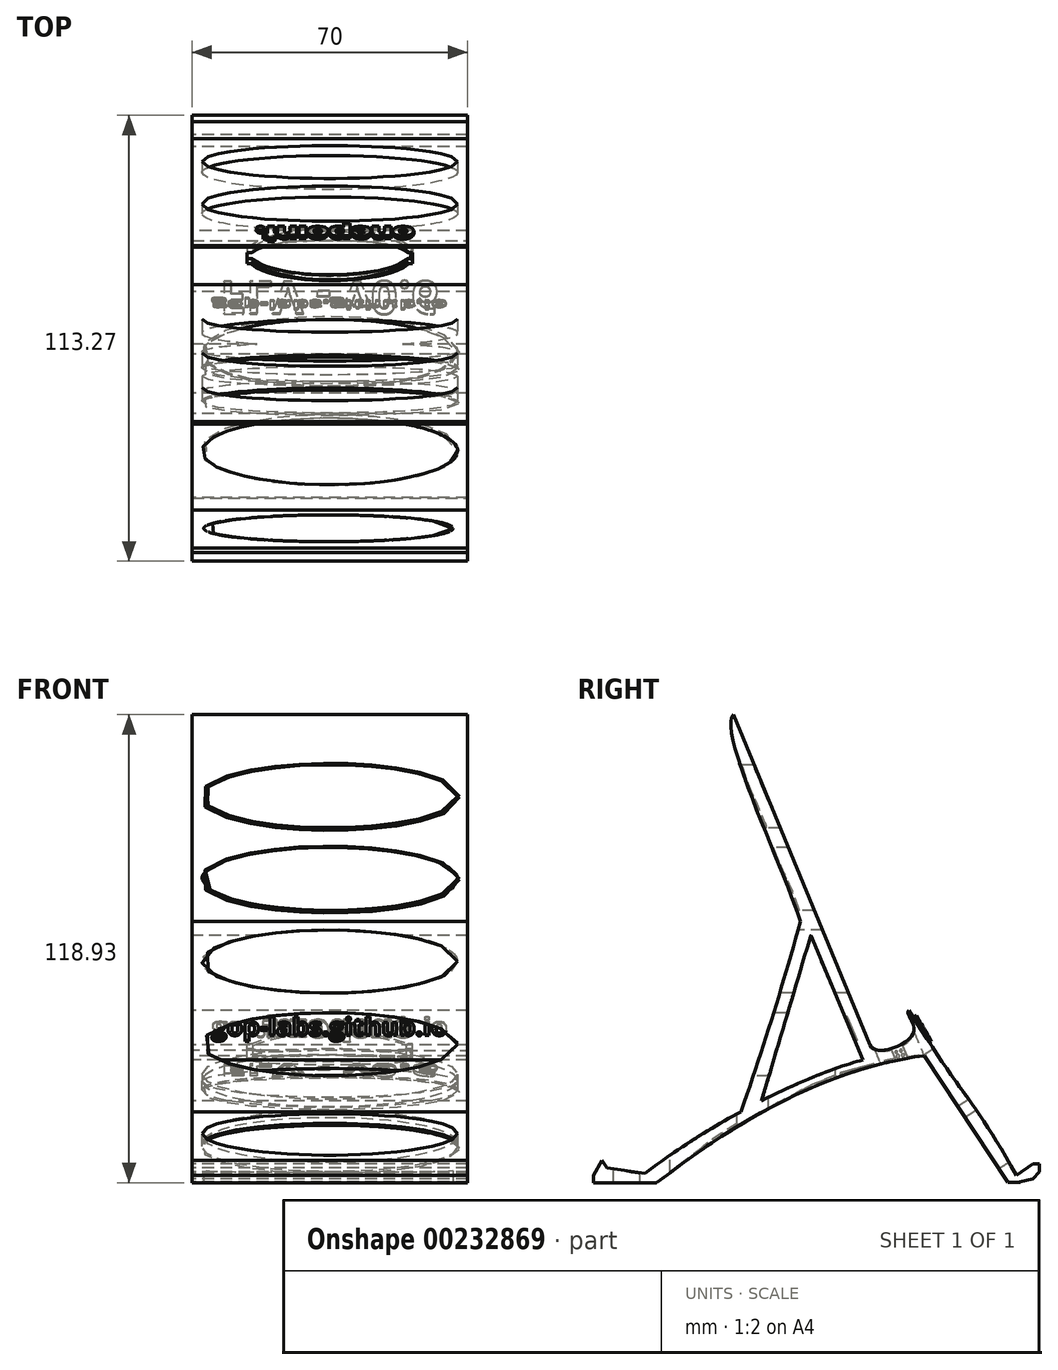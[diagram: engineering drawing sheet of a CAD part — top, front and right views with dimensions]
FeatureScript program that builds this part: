
annotation { "Feature Type Name" : "Feature", "Feature Type Description" : "" }
export const myFeature = defineFeature(function(context is Context, id is Id, definition is map)
    precondition{}
    {
        {
            var Q0;
            Q0=qCreatedBy(makeId("Right.planeOp"),FACE);
            var sketch = newSketch(context, id + "F0", { "sketchPlane" : qUnion([Q0])});
            skFitSpline(sketch, "E0", {"points": [v(42.97, 20.37) * mm, v(14.77, 64.07) * mm], "startDerivative": vector(-33.57, 62.35) * mm, "endDerivative": vector(-38.78, 64) * mm});
            skLineSegment(sketch, "E1", {"start": v(-29.92, 139.27) * mm, "end": v(4.83, 55.39) * mm});
            skFitSpline(sketch, "E2", {"points": [v(4.83, 55.39) * mm, v(15.94, 58.63) * mm, v(14.77, 64.07) * mm], "startDerivative": vector(5.7, -17.02) * mm, "endDerivative": vector(10.42, 3.26) * mm});
            skLineSegment(sketch, "E3", {"start": v(18.6, 52.58) * mm, "end": v(39.9, 20.37) * mm});
            skLineSegment(sketch, "E4", {"start": v(-10.23, 83.1) * mm, "end": v(3.1, 51.52) * mm});
            skFitSpline(sketch, "E5", {"points": [v(-29.92, 139.27) * mm, v(-12.82, 86.66) * mm], "startDerivative": vector(-12.17, -12.55) * mm, "endDerivative": vector(13.11, -40.92) * mm});
            skFitSpline(sketch, "E6", {"points": [v(3.1, 51.52) * mm, v(-55.3, 20.37) * mm], "startDerivative": vector(-34.97, -8.7) * mm, "endDerivative": vector(-63.71, -51.04) * mm});
            skFitSpline(sketch, "E7", {"points": [v(18.6, 52.58) * mm, v(-49.24, 20.37) * mm], "startDerivative": vector(-55.78, -6.95) * mm, "endDerivative": vector(-79.56, -62.3) * mm});
            skLineSegment(sketch, "E8", {"start": v(-49.24, 20.37) * mm, "end": v(-55.3, 20.37) * mm});
            skLineSegment(sketch, "E9", {"start": v(42.97, 20.37) * mm, "end": v(39.9, 20.37) * mm});
            skLineSegment(sketch, "E10", {"start": v(39.9, 20.37) * mm, "end": v(-49.24, 20.37) * mm});
            skFitSpline(sketch, "E11", {"points": [v(-10.23, 83.1) * mm, v(-22.72, 41.14) * mm], "startDerivative": vector(-11.4, -38.7) * mm, "endDerivative": vector(-11.4, -38.7) * mm});
            skFitSpline(sketch, "E12", {"points": [v(-12.82, 86.66) * mm, v(-27.98, 38.37) * mm], "startDerivative": vector(-14.28, -50.37) * mm, "endDerivative": vector(-17.92, -50.53) * mm});
            skSolve(sketch);
        }
        {
            var Q0;
            Q0=makeQuery(id+"F0.imprint","IMPRINT",FACE,{"disambiguationData":[TD([[makeQuery(id+"F0.imprint","IMPRINT",EDGE,{"derivedFrom":sQuery(id+"F0.wireOp",EDGE,"e2dd9e04-bce8-43ee-a2f2-a46b7d135692")}),-1.0]])]});
            var Q1;
            Q1=makeQuery(id+"F0.imprint","IMPRINT",FACE,{"disambiguationData":[TD([[makeQuery(id+"F0.imprint","IMPRINT",EDGE,{"derivedFrom":sQuery(id+"F0.wireOp",EDGE,"dd02e322-1caa-4adf-9807-8f987be65d11")}),1.0]])]});
            var Q2;
            Q2=makeQuery(id+"F0.imprint","IMPRINT",FACE,{"disambiguationData":[TD([[makeQuery(id+"F0.imprint","IMPRINT",EDGE,{"derivedFrom":sQuery(id+"F0.wireOp",EDGE,"E0")}),1.0]])]});
            var Q3;
            {var subQ0=sQuery(id+"F0.wireOp",EDGE,"E6");Q3=makeQuery(id+"F0.imprint","IMPRINT",FACE,{"disambiguationData":[TD([[makeQuery(id+"F0.imprint","IMPRINT",EDGE,{"derivedFrom":subQ0}),1.0]])]});}
            extrude(context, id + "F1", {"entities" : qUnion([Q0, Q1, Q2, Q3]), "depth" : 70 * mm});
        }
        {
            var Q0;
            Q0=makeQuery(id+"F1.opExtrude","SWEPT_FACE",FACE,{"disambiguationData":[OSD([sQuery(id+"F0.wireOp",EDGE,"E3")])]});
            var sketch = newSketch(context, id + "F2", { "sketchPlane" : qUnion([Q0])});
            skEllipse(sketch, "E13", {"center": v(35, 25.97) * mm, "majorRadius": 32.5 * mm, "minorRadius": 7.82 * mm, "majorAxis": v(1, 0)});
            skEllipse(sketch, "E14.0.1.0", {"center": v(35, 6.97) * mm, "majorRadius": 32.5 * mm, "minorRadius": 7.82 * mm, "majorAxis": v(1, 0)});
            skLineSegment(sketch, "E14.direction1", {"start": v(35, 25.97) * mm, "end": v(57.03, 25.97) * mm, "construction": true});
            skLineSegment(sketch, "E14.direction2", {"start": v(35, 25.97) * mm, "end": v(35, 6.97) * mm, "construction": true});
            skSolve(sketch);
        }
        {
            var Q0;
            Q0=qSketchRegion(id+"F2",true);
            var Q1;
            Q1=makeQuery(id+"F1.opExtrude","SWEPT_FACE",FACE,{"disambiguationData":[OSD([sQuery(id+"F0.wireOp",EDGE,"E0")])]});
            extrude(context, id + "F3", {"entities" : qUnion([Q0]), "operationType" : NewBodyOperationType.REMOVE, "endBound" : BoundingType.UP_TO_SURFACE, "oppositeDirection" : true, "endBoundEntityFace" : qUnion([Q1]), "depth" : 25 * mm});
        }
        {
            var Q0;
            Q0=qCreatedBy(makeId("Top.planeOp"),FACE);
            var sketch = newSketch(context, id + "F4", { "sketchPlane" : qUnion([Q0])});
            skEllipse(sketch, "E15", {"center": v(35, -37.48) * mm, "majorRadius": 32.5 * mm, "minorRadius": 8.5 * mm, "majorAxis": v(1, 0)});
            skEllipse(sketch, "E16.0.1.0", {"center": v(35, -12.48) * mm, "majorRadius": 32.5 * mm, "minorRadius": 8.5 * mm, "majorAxis": v(1, 0)});
            skLineSegment(sketch, "E16.direction1", {"start": v(35, -37.48) * mm, "end": v(60, -37.48) * mm, "construction": true});
            skLineSegment(sketch, "E16.direction2", {"start": v(35, -37.48) * mm, "end": v(35, -12.48) * mm, "construction": true});
            skSolve(sketch);
        }
        {
            var Q0;
            Q0=makeQuery(id+"F4.imprint","IMPRINT",FACE,{"disambiguationData":[TD([[makeQuery(id+"F4.imprint","IMPRINT",EDGE,{"derivedFrom":sQuery(id+"F4.wireOp",EDGE,"E16.0.1.0")}),1.0]])]});
            var Q1;
            Q1=makeQuery(id+"F4.imprint","IMPRINT",FACE,{"disambiguationData":[TD([[makeQuery(id+"F4.imprint","IMPRINT",EDGE,{"derivedFrom":sQuery(id+"F4.wireOp",EDGE,"E16.0.2.0")}),1.0]])]});
            var Q2;
            Q2=makeQuery(id+"F1.opExtrude","SWEPT_FACE",FACE,{"disambiguationData":[OSD([sQuery(id+"F0.wireOp",EDGE,"E6")])]});
            extrude(context, id + "F5", {"entities" : qUnion([Q0, Q1]), "operationType" : NewBodyOperationType.REMOVE, "endBound" : BoundingType.UP_TO_SURFACE, "endBoundEntityFace" : qUnion([Q2]), "depth" : 25 * mm});
        }
        {
            var Q0;
            Q0=qCreatedBy(makeId("Front.planeOp"),FACE);
            cPlane(context, id + "F6", {"entities" : qUnion([Q0]), "cplaneType" : CPlaneType.OFFSET, "offset" : 70 * mm, "width" : 150 * mm, "height" : 150 * mm});
        }
        {
            var Q0;
            Q0=qCreatedBy(id+"F6.planeOp",FACE);
            var sketch = newSketch(context, id + "F7", { "sketchPlane" : qUnion([Q0])});
            skEllipse(sketch, "E17", {"center": v(35, 118.52) * mm, "majorRadius": 32.5 * mm, "minorRadius": 8 * mm, "majorAxis": v(1, 0)});
            skEllipse(sketch, "E18.0.1.0", {"center": v(35, 97.52) * mm, "majorRadius": 32.5 * mm, "minorRadius": 8 * mm, "majorAxis": v(1, 0)});
            skEllipse(sketch, "E18.0.2.0", {"center": v(35, 76.52) * mm, "majorRadius": 32.5 * mm, "minorRadius": 8 * mm, "majorAxis": v(1, 0)});
            skEllipse(sketch, "E18.0.3.0", {"center": v(35, 55.52) * mm, "majorRadius": 32.5 * mm, "minorRadius": 8 * mm, "majorAxis": v(1, 0)});
            skEllipse(sketch, "E18.0.4.0", {"center": v(35, 34.52) * mm, "majorRadius": 32.5 * mm, "minorRadius": 8 * mm, "majorAxis": v(1, 0)});
            skEllipse(sketch, "E18.0.5.0", {"center": v(35, 13.52) * mm, "majorRadius": 32.5 * mm, "minorRadius": 8 * mm, "majorAxis": v(1, 0)});
            skLineSegment(sketch, "E18.direction1", {"start": v(35, 118.52) * mm, "end": v(60, 118.52) * mm, "construction": true});
            skLineSegment(sketch, "E18.direction2", {"start": v(35, 118.52) * mm, "end": v(35, 97.52) * mm, "construction": true});
            skSolve(sketch);
        }
        {
            var Q0;
            Q0=makeQuery(id+"F7.imprint","IMPRINT",FACE,{"disambiguationData":[TD([[makeQuery(id+"F7.imprint","IMPRINT",EDGE,{"derivedFrom":sQuery(id+"F7.wireOp",EDGE,"E18.0.3.0")}),1.0]])]});
            var Q1;
            Q1=makeQuery(id+"F1.opExtrude","SWEPT_FACE",FACE,{"disambiguationData":[OSD([sQuery(id+"F0.wireOp",EDGE,"E11")])]});
            extrude(context, id + "F8", {"entities" : qUnion([Q0]), "operationType" : NewBodyOperationType.REMOVE, "endBound" : BoundingType.UP_TO_SURFACE, "oppositeDirection" : true, "endBoundEntityFace" : qUnion([Q1]), "depth" : 25 * mm});
        }
        {
            var Q0;
            Q0=makeQuery(id+"F7.imprint","IMPRINT",FACE,{"disambiguationData":[TD([[makeQuery(id+"F7.imprint","IMPRINT",EDGE,{"derivedFrom":sQuery(id+"F7.wireOp",EDGE,"E17")}),1.0]])]});
            var Q1;
            Q1=makeQuery(id+"F7.imprint","IMPRINT",FACE,{"disambiguationData":[TD([[makeQuery(id+"F7.imprint","IMPRINT",EDGE,{"derivedFrom":sQuery(id+"F7.wireOp",EDGE,"E18.0.1.0")}),1.0]])]});
            var Q2;
            Q2=makeQuery(id+"F7.imprint","IMPRINT",FACE,{"disambiguationData":[TD([[makeQuery(id+"F7.imprint","IMPRINT",EDGE,{"derivedFrom":sQuery(id+"F7.wireOp",EDGE,"E18.0.2.0")}),1.0]])]});
            var Q3;
            Q3=makeQuery(id+"F1.opExtrude","SWEPT_FACE",FACE,{"disambiguationData":[OSD([sQuery(id+"F0.wireOp",EDGE,"E1")])]});
            extrude(context, id + "F9", {"entities" : qUnion([Q0, Q1, Q2]), "operationType" : NewBodyOperationType.REMOVE, "endBound" : BoundingType.UP_TO_SURFACE, "oppositeDirection" : true, "endBoundEntityFace" : qUnion([Q3]), "depth" : 25 * mm});
        }
        {
            var Q0;
            Q0=makeQuery(id+"F1.opExtrude","SWEPT_FACE",FACE,{"disambiguationData":[OSD([sQuery(id+"F0.wireOp",EDGE,"E1")])]});
            var Q1;
            Q1=makeQuery(id+"F1.opExtrude","SWEPT_EDGE",EDGE,{"disambiguationData":[OSD([sQuery(id+"F0.wireOp",EDGE,"E1"),sQuery(id+"F0.wireOp",EDGE,"E5")])]});
            cPlane(context, id + "F10", {"entities" : qUnion([Q0, Q1]), "cplaneType" : CPlaneType.LINE_ANGLE, "offset" : 25 * mm, "angle" : 90 * degree, "width" : 150 * mm, "height" : 150 * mm});
        }
        {
            var Q0;
            Q0=qCreatedBy(id+"F10.planeOp",FACE);
            var sketch = newSketch(context, id + "F11", { "sketchPlane" : qUnion([Q0])});
            skEllipse(sketch, "E19", {"center": v(35, 31.76) * mm, "majorRadius": 20.25 * mm, "minorRadius": 5.5 * mm, "majorAxis": v(-1, 0)});
            skLineSegment(sketch, "E20.bottom", {"start": v(14, 30.26) * mm, "end": v(56, 30.26) * mm});
            skLineSegment(sketch, "E20.top", {"start": v(14, 33.26) * mm, "end": v(56, 33.26) * mm});
            skLineSegment(sketch, "E20.left", {"start": v(14, 30.26) * mm, "end": v(14, 33.26) * mm});
            skLineSegment(sketch, "E20.right", {"start": v(56, 30.26) * mm, "end": v(56, 33.26) * mm});
            skSolve(sketch);
        }
        {
            var Q0;
            Q0=qSketchRegion(id+"F11",true);
            var Q1;
            Q1=makeQuery(id+"F1.opExtrude","SWEPT_FACE",FACE,{"disambiguationData":[OSD([sQuery(id+"F0.wireOp",EDGE,"E7")])]});
            extrude(context, id + "F12", {"entities" : qUnion([Q0]), "operationType" : NewBodyOperationType.REMOVE, "endBound" : BoundingType.THROUGH_ALL, "oppositeDirection" : true, "endBoundEntityFace" : qUnion([Q1]), "depth" : 25 * mm});
        }
        {
            var Q0;
            Q0=makeQuery(id+"F3.boolean.opBoolean","COPY",EDGE,{"derivedFrom":makeQuery(id+"F3.opExtrude","TWEAK_EDGE",EDGE,{"derivedFrom":[makeQuery(id+"F1.opExtrude","SWEPT_FACE",FACE,{"disambiguationData":[OSD([sQuery(id+"F0.wireOp",EDGE,"E0")])]}),makeQuery(id+"F2.imprint","IMPRINT",EDGE,{"derivedFrom":sQuery(id+"F2.wireOp",EDGE,"E13")})]})});
            var Q1;
            Q1=makeQuery(id+"F3.boolean.opBoolean","COPY",EDGE,{"derivedFrom":makeQuery(id+"F3.opExtrude","TWEAK_EDGE",EDGE,{"derivedFrom":[makeQuery(id+"F1.opExtrude","SWEPT_FACE",FACE,{"disambiguationData":[OSD([sQuery(id+"F0.wireOp",EDGE,"E0")])]}),makeQuery(id+"F2.imprint","IMPRINT",EDGE,{"derivedFrom":sQuery(id+"F2.wireOp",EDGE,"E14.0.1.0")})]})});
            var Q2;
            Q2=makeQuery(id+"F3.boolean.opBoolean","COPY",EDGE,{"derivedFrom":makeQuery(id+"F3.opExtrude","TWEAK_EDGE",EDGE,{"derivedFrom":[makeQuery(id+"F1.opExtrude","SWEPT_FACE",FACE,{"disambiguationData":[OSD([sQuery(id+"F0.wireOp",EDGE,"E0")])]}),makeQuery(id+"F2.imprint","IMPRINT",EDGE,{"derivedFrom":sQuery(id+"F2.wireOp",EDGE,"E14.0.2.0")})]})});
            var Q3;
            Q3=makeQuery(id+"F3.boolean.opBoolean","COPY",EDGE,{"derivedFrom":makeQuery(id+"F3.opExtrude","CAP_EDGE",EDGE,{"disambiguationData":[OSD([sQuery(id+"F2.wireOp",EDGE,"E13")])],"isStart":true})});
            var Q4;
            Q4=makeQuery(id+"F3.boolean.opBoolean","COPY",EDGE,{"derivedFrom":makeQuery(id+"F3.opExtrude","CAP_EDGE",EDGE,{"disambiguationData":[OSD([sQuery(id+"F2.wireOp",EDGE,"E14.0.1.0")])],"isStart":true})});
            var Q5;
            Q5=makeQuery(id+"F3.boolean.opBoolean","COPY",EDGE,{"derivedFrom":makeQuery(id+"F3.opExtrude","CAP_EDGE",EDGE,{"disambiguationData":[OSD([sQuery(id+"F2.wireOp",EDGE,"E14.0.2.0")])],"isStart":true})});
            var Q6;
            Q6=makeQuery(id+"F8.boolean.opBoolean","INTERSECT",EDGE,{"derivedFrom":[makeQuery(id+"F1.opExtrude","SWEPT_FACE",FACE,{"disambiguationData":[OSD([sQuery(id+"F0.wireOp",EDGE,"61fd75d5-24df-4c68-a095-90f6d82b9ead")])]}),makeQuery(id+"F8.opExtrude","SWEPT_FACE",FACE,{"disambiguationData":[OSD([sQuery(id+"F7.wireOp",EDGE,"E18.0.3.0")])]})]});
            var Q7;
            Q7=makeQuery(id+"F8.boolean.opBoolean","COPY",EDGE,{"derivedFrom":makeQuery(id+"F8.opExtrude","CAP_EDGE",EDGE,{"disambiguationData":[OSD([sQuery(id+"F7.wireOp",EDGE,"E18.0.3.0")])],"isStart":false})});
            var Q8;
            Q8=makeQuery(id+"F8.boolean.opBoolean","INTERSECT",EDGE,{"derivedFrom":[makeQuery(id+"F1.opExtrude","SWEPT_FACE",FACE,{"disambiguationData":[OSD([sQuery(id+"F0.wireOp",EDGE,"61fd75d5-24df-4c68-a095-90f6d82b9ead")])]}),makeQuery(id+"F8.opExtrude","SWEPT_FACE",FACE,{"disambiguationData":[OSD([sQuery(id+"F7.wireOp",EDGE,"E18.0.4.0")])]})]});
            var Q9;
            {var subQ0=sQuery(id+"F0.wireOp",EDGE,"5998eb2a-c125-4484-9ba4-89ed062cae3a");var subQ1=sQuery(id+"F0.wireOp",EDGE,"E7");var subQ2=sQuery(id+"F7.wireOp",EDGE,"E18.0.4.0");Q9=makeQuery(id+"F8.boolean.opBoolean","COPY",EDGE,{"disambiguationData":[TD([makeQuery(id+"F1.opExtrude","SWEPT_FACE",FACE,{"disambiguationData":[OSD([subQ0]),TDD([makeQuery(id+"F0.imprint","IMPRINT",EDGE,{"disambiguationData":[TD([[makeQuery(id+"F0.imprint","INTERSECT",VERTEX,{"derivedFrom":[subQ0,sQuery(id+"F0.wireOp",EDGE,"umK4nLRB-749r-FOEl-6r3i-m92kNIwFStfI")]}),-1.0]])],"derivedFrom":subQ0})])]}),makeQuery(id+"F1.opExtrude","SWEPT_FACE",FACE,{"disambiguationData":[OSD([subQ1])]}),makeQuery(id+"F8.opExtrude","SWEPT_FACE",FACE,{"disambiguationData":[OSD([subQ2])]}),makeQuery(id+"F8.opExtrude","CAP_FACE",FACE,{"disambiguationData":[OSD([subQ2])],"isStart":false})])],"derivedFrom":makeQuery(id+"F8.opExtrude","CAP_EDGE",EDGE,{"disambiguationData":[OSD([subQ2])],"isStart":false})});}
            var Q10;
            Q10=makeQuery(id+"F8.boolean.opBoolean","INTERSECT",EDGE,{"derivedFrom":[makeQuery(id+"F1.opExtrude","SWEPT_FACE",FACE,{"disambiguationData":[OSD([sQuery(id+"F0.wireOp",EDGE,"61fd75d5-24df-4c68-a095-90f6d82b9ead")])]}),makeQuery(id+"F8.opExtrude","SWEPT_FACE",FACE,{"disambiguationData":[OSD([sQuery(id+"F7.wireOp",EDGE,"E18.0.5.0")])]})]});
            var Q11;
            Q11=makeQuery(id+"F8.boolean.opBoolean","COPY",EDGE,{"derivedFrom":makeQuery(id+"F8.opExtrude","CAP_EDGE",EDGE,{"disambiguationData":[OSD([sQuery(id+"F7.wireOp",EDGE,"E18.0.5.0")])],"isStart":false})});
            var Q12;
            {var subQ0=sQuery(id+"F0.wireOp",EDGE,"5998eb2a-c125-4484-9ba4-89ed062cae3a");Q12=makeQuery(id+"F9.boolean.opBoolean","INTERSECT",EDGE,{"derivedFrom":[makeQuery(id+"F1.opExtrude","SWEPT_FACE",FACE,{"disambiguationData":[OSD([subQ0]),TDD([makeQuery(id+"F0.imprint","IMPRINT",EDGE,{"disambiguationData":[TD([[makeQuery(id+"F0.imprint","INTERSECT",VERTEX,{"derivedFrom":[subQ0,sQuery(id+"F0.wireOp",EDGE,"E4")]}),1.0]])],"derivedFrom":subQ0})])]}),makeQuery(id+"F9.opExtrude","SWEPT_FACE",FACE,{"disambiguationData":[OSD([sQuery(id+"F7.wireOp",EDGE,"E18.0.2.0")])]})]});}
            var Q13;
            Q13=makeQuery(id+"F9.boolean.opBoolean","INTERSECT",EDGE,{"derivedFrom":[makeQuery(id+"F1.opExtrude","SWEPT_FACE",FACE,{"disambiguationData":[OSD([sQuery(id+"F0.wireOp",EDGE,"61fd75d5-24df-4c68-a095-90f6d82b9ead")])]}),makeQuery(id+"F9.opExtrude","SWEPT_FACE",FACE,{"disambiguationData":[OSD([sQuery(id+"F7.wireOp",EDGE,"E18.0.2.0")])]})]});
            var Q14;
            Q14=makeQuery(id+"F5.boolean.opBoolean","COPY",EDGE,{"derivedFrom":makeQuery(id+"F5.opExtrude","TWEAK_EDGE",EDGE,{"derivedFrom":[makeQuery(id+"F1.opExtrude","SWEPT_FACE",FACE,{"disambiguationData":[OSD([sQuery(id+"F0.wireOp",EDGE,"E6")])]}),makeQuery(id+"F4.imprint","IMPRINT",EDGE,{"derivedFrom":sQuery(id+"F4.wireOp",EDGE,"E16.0.1.0")})]})});
            var Q15;
            Q15=makeQuery(id+"F5.boolean.opBoolean","INTERSECT",EDGE,{"derivedFrom":[makeQuery(id+"F1.opExtrude","SWEPT_FACE",FACE,{"disambiguationData":[OSD([sQuery(id+"F0.wireOp",EDGE,"E7")])]}),makeQuery(id+"F5.opExtrude","SWEPT_FACE",FACE,{"disambiguationData":[OSD([sQuery(id+"F4.wireOp",EDGE,"E16.0.1.0")])]})]});
            var Q16;
            Q16=makeQuery(id+"F5.boolean.opBoolean","INTERSECT",EDGE,{"derivedFrom":[makeQuery(id+"F1.opExtrude","SWEPT_FACE",FACE,{"disambiguationData":[OSD([sQuery(id+"F0.wireOp",EDGE,"E7")])]}),makeQuery(id+"F5.opExtrude","SWEPT_FACE",FACE,{"disambiguationData":[OSD([sQuery(id+"F4.wireOp",EDGE,"E15")])]})]});
            var Q17;
            Q17=makeQuery(id+"F5.boolean.opBoolean","COPY",EDGE,{"derivedFrom":makeQuery(id+"F5.opExtrude","TWEAK_EDGE",EDGE,{"derivedFrom":[makeQuery(id+"F1.opExtrude","SWEPT_FACE",FACE,{"disambiguationData":[OSD([sQuery(id+"F0.wireOp",EDGE,"E6")])]}),makeQuery(id+"F4.imprint","IMPRINT",EDGE,{"derivedFrom":sQuery(id+"F4.wireOp",EDGE,"E15")})]})});
            var Q18;
            Q18=makeQuery(id+"F9.boolean.opBoolean","COPY",EDGE,{"derivedFrom":makeQuery(id+"F9.opExtrude","TWEAK_EDGE",EDGE,{"derivedFrom":[makeQuery(id+"F1.opExtrude","SWEPT_FACE",FACE,{"disambiguationData":[OSD([sQuery(id+"F0.wireOp",EDGE,"E1")])]}),makeQuery(id+"F7.imprint","IMPRINT",EDGE,{"derivedFrom":sQuery(id+"F7.wireOp",EDGE,"E18.0.2.0")})]})});
            var Q19;
            Q19=makeQuery(id+"F9.boolean.opBoolean","COPY",EDGE,{"derivedFrom":makeQuery(id+"F9.opExtrude","TWEAK_EDGE",EDGE,{"derivedFrom":[makeQuery(id+"F1.opExtrude","SWEPT_FACE",FACE,{"disambiguationData":[OSD([sQuery(id+"F0.wireOp",EDGE,"E1")])]}),makeQuery(id+"F7.imprint","IMPRINT",EDGE,{"derivedFrom":sQuery(id+"F7.wireOp",EDGE,"E18.0.1.0")})]})});
            var Q20;
            Q20=makeQuery(id+"F9.boolean.opBoolean","INTERSECT",EDGE,{"derivedFrom":[makeQuery(id+"F1.opExtrude","SWEPT_FACE",FACE,{"disambiguationData":[OSD([sQuery(id+"F0.wireOp",EDGE,"E5")])]}),makeQuery(id+"F9.opExtrude","SWEPT_FACE",FACE,{"disambiguationData":[OSD([sQuery(id+"F7.wireOp",EDGE,"E18.0.1.0")])]})]});
            var Q21;
            Q21=makeQuery(id+"F9.boolean.opBoolean","INTERSECT",EDGE,{"derivedFrom":[makeQuery(id+"F1.opExtrude","SWEPT_FACE",FACE,{"disambiguationData":[OSD([sQuery(id+"F0.wireOp",EDGE,"E5")])]}),makeQuery(id+"F9.opExtrude","SWEPT_FACE",FACE,{"disambiguationData":[OSD([sQuery(id+"F7.wireOp",EDGE,"E17")])]})]});
            var Q22;
            Q22=makeQuery(id+"F9.boolean.opBoolean","COPY",EDGE,{"derivedFrom":makeQuery(id+"F9.opExtrude","TWEAK_EDGE",EDGE,{"derivedFrom":[makeQuery(id+"F1.opExtrude","SWEPT_FACE",FACE,{"disambiguationData":[OSD([sQuery(id+"F0.wireOp",EDGE,"E1")])]}),makeQuery(id+"F7.imprint","IMPRINT",EDGE,{"derivedFrom":sQuery(id+"F7.wireOp",EDGE,"E17")})]})});
            fillet(context, id + "F13", {"entities" : qUnion([Q0, Q1, Q2, Q3, Q4, Q5, Q6, Q7, Q8, Q9, Q10, Q11, Q12, Q13, Q14, Q15, Q16, Q17, Q18, Q19, Q20, Q21, Q22]), "radius" : 0.5 * mm, "tangentPropagation" : true, "allowEdgeOverflow" : false});
        }
        {
            var Q0;
            Q0=makeQuery(id+"F1.opExtrude","SWEPT_EDGE",EDGE,{"disambiguationData":[OSD([sQuery(id+"F0.wireOp",EDGE,"E0"),sQuery(id+"F0.wireOp",EDGE,"E2")])]});
            cPlane(context, id + "F14", {"entities" : qUnion([Q0]), "cplaneType" : CPlaneType.LINE_ANGLE, "offset" : 25 * mm, "angle" : 150 * degree, "width" : 150 * mm, "height" : 150 * mm});
        }
        {
            var Q0;
            Q0=qCreatedBy(id+"F14.planeOp",FACE);
            var sketch = newSketch(context, id + "F15", { "sketchPlane" : qUnion([Q0])});
            skLineSegment(sketch, "E21", {"start": v(-54.12, 39.93) * mm, "end": v(-54.9, 40.17) * mm});
            skLineSegment(sketch, "E22", {"start": v(-54.9, 40.17) * mm, "end": v(-55.54, 40.6) * mm});
            skLineSegment(sketch, "E23", {"start": v(-55.54, 40.6) * mm, "end": v(-56.02, 41.2) * mm});
            skLineSegment(sketch, "E24", {"start": v(-56.02, 41.2) * mm, "end": v(-56.3, 41.94) * mm});
            skLineSegment(sketch, "E25", {"start": v(-56.3, 41.94) * mm, "end": v(-56.33, 42.13) * mm});
            skLineSegment(sketch, "E26", {"start": v(-56.33, 42.13) * mm, "end": v(-56.34, 42.37) * mm});
            skLineSegment(sketch, "E27", {"start": v(-56.34, 42.62) * mm, "end": v(-56.32, 42.83) * mm});
            skLineSegment(sketch, "E28", {"start": v(-56.32, 42.83) * mm, "end": v(-56.06, 43.6) * mm});
            skLineSegment(sketch, "E29", {"start": v(-56.06, 43.6) * mm, "end": v(-55.56, 44.26) * mm});
            skLineSegment(sketch, "E30", {"start": v(-55.56, 44.26) * mm, "end": v(-55.18, 44.57) * mm});
            skLineSegment(sketch, "E31", {"start": v(-55.18, 44.57) * mm, "end": v(-54.75, 44.8) * mm});
            skLineSegment(sketch, "E32", {"start": v(-54.75, 44.8) * mm, "end": v(-54.28, 44.94) * mm});
            skLineSegment(sketch, "E33", {"start": v(-54.28, 44.94) * mm, "end": v(-53.77, 45) * mm});
            skLineSegment(sketch, "E34", {"start": v(-53.77, 45) * mm, "end": v(-53.19, 44.98) * mm});
            skLineSegment(sketch, "E35", {"start": v(-53.19, 44.98) * mm, "end": v(-52.64, 44.84) * mm});
            skLineSegment(sketch, "E36", {"start": v(-52.64, 44.84) * mm, "end": v(-52.15, 44.6) * mm});
            skLineSegment(sketch, "E37", {"start": v(-52.15, 44.6) * mm, "end": v(-51.7, 44.26) * mm});
            skLineSegment(sketch, "E38", {"start": v(-51.7, 44.26) * mm, "end": v(-51.23, 43.63) * mm});
            skLineSegment(sketch, "E39", {"start": v(-51.23, 43.63) * mm, "end": v(-50.98, 42.9) * mm});
            skLineSegment(sketch, "E40", {"start": v(-50.98, 42.9) * mm, "end": v(-50.95, 42.7) * mm});
            skLineSegment(sketch, "E41", {"start": v(-50.95, 42.7) * mm, "end": v(-50.95, 42.45) * mm});
            skLineSegment(sketch, "E42", {"start": v(-50.95, 42.45) * mm, "end": v(-50.96, 42.2) * mm});
            skLineSegment(sketch, "E43", {"start": v(-50.96, 42.2) * mm, "end": v(-50.99, 42) * mm});
            skLineSegment(sketch, "E44", {"start": v(-50.99, 42) * mm, "end": v(-51.26, 41.25) * mm});
            skLineSegment(sketch, "E45", {"start": v(-51.26, 41.25) * mm, "end": v(-51.73, 40.64) * mm});
            skLineSegment(sketch, "E46", {"start": v(-51.73, 40.64) * mm, "end": v(-52.37, 40.19) * mm});
            skLineSegment(sketch, "E47", {"start": v(-52.37, 40.19) * mm, "end": v(-53.14, 39.94) * mm});
            skLineSegment(sketch, "E48", {"start": v(-53.14, 39.94) * mm, "end": v(-53.63, 39.9) * mm});
            skLineSegment(sketch, "E49", {"start": v(-53.63, 39.9) * mm, "end": v(-54.12, 39.93) * mm});
            skLineSegment(sketch, "E50", {"start": v(-54.12, 39.93) * mm, "end": v(-54.12, 39.93) * mm});
            skLineSegment(sketch, "E51", {"start": v(-53.38, 41.4) * mm, "end": v(-53.15, 41.5) * mm});
            skLineSegment(sketch, "E52", {"start": v(-53.15, 41.5) * mm, "end": v(-52.96, 41.63) * mm});
            skLineSegment(sketch, "E53", {"start": v(-52.96, 41.63) * mm, "end": v(-52.8, 41.82) * mm});
            skLineSegment(sketch, "E54", {"start": v(-52.8, 41.82) * mm, "end": v(-52.7, 42.06) * mm});
            skLineSegment(sketch, "E55", {"start": v(-52.7, 42.06) * mm, "end": v(-52.63, 42.42) * mm});
            skLineSegment(sketch, "E56", {"start": v(-52.63, 42.42) * mm, "end": v(-52.67, 42.77) * mm});
            skLineSegment(sketch, "E57", {"start": v(-52.67, 42.77) * mm, "end": v(-52.8, 43.04) * mm});
            skLineSegment(sketch, "E58", {"start": v(-52.8, 43.04) * mm, "end": v(-52.97, 43.26) * mm});
            skLineSegment(sketch, "E59", {"start": v(-52.97, 43.26) * mm, "end": v(-53.2, 43.42) * mm});
            skLineSegment(sketch, "E60", {"start": v(-53.2, 43.42) * mm, "end": v(-53.46, 43.52) * mm});
            skLineSegment(sketch, "E61", {"start": v(-53.46, 43.52) * mm, "end": v(-53.57, 43.54) * mm});
            skLineSegment(sketch, "E62", {"start": v(-53.57, 43.54) * mm, "end": v(-53.66, 43.55) * mm});
            skLineSegment(sketch, "E63", {"start": v(-53.66, 43.55) * mm, "end": v(-53.88, 43.52) * mm});
            skLineSegment(sketch, "E64", {"start": v(-53.88, 43.52) * mm, "end": v(-54.1, 43.44) * mm});
            skLineSegment(sketch, "E65", {"start": v(-54.1, 43.44) * mm, "end": v(-54.28, 43.32) * mm});
            skLineSegment(sketch, "E66", {"start": v(-54.28, 43.32) * mm, "end": v(-54.43, 43.16) * mm});
            skLineSegment(sketch, "E67", {"start": v(-54.43, 43.16) * mm, "end": v(-54.55, 42.97) * mm});
            skLineSegment(sketch, "E68", {"start": v(-54.55, 42.97) * mm, "end": v(-54.62, 42.76) * mm});
            skLineSegment(sketch, "E69", {"start": v(-54.62, 42.76) * mm, "end": v(-54.65, 42.62) * mm});
            skLineSegment(sketch, "E70", {"start": v(-54.65, 42.62) * mm, "end": v(-54.66, 42.46) * mm});
            skLineSegment(sketch, "E71", {"start": v(-54.66, 42.46) * mm, "end": v(-54.65, 42.3) * mm});
            skLineSegment(sketch, "E72", {"start": v(-54.65, 42.3) * mm, "end": v(-54.62, 42.18) * mm});
            skLineSegment(sketch, "E73", {"start": v(-54.62, 42.18) * mm, "end": v(-54.52, 41.9) * mm});
            skLineSegment(sketch, "E74", {"start": v(-54.52, 41.9) * mm, "end": v(-54.35, 41.68) * mm});
            skLineSegment(sketch, "E75", {"start": v(-54.35, 41.68) * mm, "end": v(-54.14, 41.5) * mm});
            skLineSegment(sketch, "E76", {"start": v(-54.14, 41.5) * mm, "end": v(-53.89, 41.4) * mm});
            skLineSegment(sketch, "E77", {"start": v(-53.89, 41.4) * mm, "end": v(-53.64, 41.37) * mm});
            skLineSegment(sketch, "E78", {"start": v(-53.64, 41.37) * mm, "end": v(-53.38, 41.4) * mm});
            skLineSegment(sketch, "E79", {"start": v(-53.38, 41.4) * mm, "end": v(-53.38, 41.4) * mm});
            skLineSegment(sketch, "E80", {"start": v(-50.6, 42.43) * mm, "end": v(-50.6, 44.87) * mm});
            skLineSegment(sketch, "E81", {"start": v(-50.6, 44.87) * mm, "end": v(-48.87, 44.87) * mm});
            skLineSegment(sketch, "E82", {"start": v(-48.87, 44.87) * mm, "end": v(-48.87, 44.24) * mm});
            skLineSegment(sketch, "E83", {"start": v(-48.87, 44.24) * mm, "end": v(-48.68, 44.42) * mm});
            skLineSegment(sketch, "E84", {"start": v(-48.68, 44.42) * mm, "end": v(-48.43, 44.66) * mm});
            skLineSegment(sketch, "E85", {"start": v(-48.43, 44.66) * mm, "end": v(-48.16, 44.81) * mm});
            skLineSegment(sketch, "E86", {"start": v(-48.16, 44.81) * mm, "end": v(-47.8, 44.94) * mm});
            skLineSegment(sketch, "E87", {"start": v(-47.8, 44.94) * mm, "end": v(-47.4, 44.99) * mm});
            skLineSegment(sketch, "E88", {"start": v(-47.4, 44.99) * mm, "end": v(-47.01, 44.95) * mm});
            skLineSegment(sketch, "E89", {"start": v(-47.01, 44.95) * mm, "end": v(-46.64, 44.83) * mm});
            skLineSegment(sketch, "E90", {"start": v(-46.64, 44.83) * mm, "end": v(-46.33, 44.63) * mm});
            skLineSegment(sketch, "E91", {"start": v(-46.33, 44.63) * mm, "end": v(-46.1, 44.38) * mm});
            skLineSegment(sketch, "E92", {"start": v(-46.1, 44.38) * mm, "end": v(-45.92, 44.06) * mm});
            skLineSegment(sketch, "E93", {"start": v(-45.92, 44.06) * mm, "end": v(-45.8, 43.66) * mm});
            skLineSegment(sketch, "E94", {"start": v(-45.8, 43.66) * mm, "end": v(-45.78, 43.6) * mm});
            skLineSegment(sketch, "E95", {"start": v(-45.78, 43.6) * mm, "end": v(-45.77, 43.52) * mm});
            skLineSegment(sketch, "E96", {"start": v(-45.77, 43.52) * mm, "end": v(-45.77, 43.4) * mm});
            skLineSegment(sketch, "E97", {"start": v(-45.77, 43.4) * mm, "end": v(-45.76, 43.24) * mm});
            skLineSegment(sketch, "E98", {"start": v(-45.76, 43.24) * mm, "end": v(-45.76, 43) * mm});
            skLineSegment(sketch, "E99", {"start": v(-45.76, 43) * mm, "end": v(-45.76, 42.69) * mm});
            skLineSegment(sketch, "E100", {"start": v(-45.76, 42.69) * mm, "end": v(-45.75, 42.27) * mm});
            skLineSegment(sketch, "E101", {"start": v(-45.75, 42.27) * mm, "end": v(-45.75, 41.75) * mm});
            skLineSegment(sketch, "E102", {"start": v(-45.75, 41.75) * mm, "end": v(-45.75, 39.99) * mm});
            skLineSegment(sketch, "E103", {"start": v(-45.75, 39.99) * mm, "end": v(-47.48, 39.99) * mm});
            skLineSegment(sketch, "E104", {"start": v(-47.48, 39.99) * mm, "end": v(-47.48, 41.4) * mm});
            skLineSegment(sketch, "E105", {"start": v(-47.48, 41.4) * mm, "end": v(-47.48, 41.88) * mm});
            skLineSegment(sketch, "E106", {"start": v(-47.48, 41.88) * mm, "end": v(-47.49, 42.23) * mm});
            skLineSegment(sketch, "E107", {"start": v(-47.49, 42.23) * mm, "end": v(-47.5, 42.49) * mm});
            skLineSegment(sketch, "E108", {"start": v(-47.5, 42.49) * mm, "end": v(-47.5, 42.67) * mm});
            skLineSegment(sketch, "E109", {"start": v(-47.5, 42.67) * mm, "end": v(-47.5, 42.79) * mm});
            skLineSegment(sketch, "E110", {"start": v(-47.5, 42.79) * mm, "end": v(-47.5, 42.87) * mm});
            skLineSegment(sketch, "E111", {"start": v(-47.5, 42.87) * mm, "end": v(-47.52, 42.92) * mm});
            skLineSegment(sketch, "E112", {"start": v(-47.52, 42.92) * mm, "end": v(-47.53, 42.96) * mm});
            skLineSegment(sketch, "E113", {"start": v(-47.53, 42.96) * mm, "end": v(-47.62, 43.15) * mm});
            skLineSegment(sketch, "E114", {"start": v(-47.62, 43.15) * mm, "end": v(-47.74, 43.3) * mm});
            skLineSegment(sketch, "E115", {"start": v(-47.74, 43.3) * mm, "end": v(-47.9, 43.4) * mm});
            skLineSegment(sketch, "E116", {"start": v(-47.9, 43.4) * mm, "end": v(-48.1, 43.44) * mm});
            skLineSegment(sketch, "E117", {"start": v(-48.1, 43.44) * mm, "end": v(-48.33, 43.42) * mm});
            skLineSegment(sketch, "E118", {"start": v(-48.33, 43.42) * mm, "end": v(-48.53, 43.34) * mm});
            skLineSegment(sketch, "E119", {"start": v(-48.53, 43.34) * mm, "end": v(-48.7, 43.19) * mm});
            skLineSegment(sketch, "E120", {"start": v(-48.7, 43.19) * mm, "end": v(-48.82, 42.98) * mm});
            skLineSegment(sketch, "E121", {"start": v(-48.82, 42.98) * mm, "end": v(-48.83, 42.94) * mm});
            skLineSegment(sketch, "E122", {"start": v(-48.83, 42.94) * mm, "end": v(-48.84, 42.9) * mm});
            skLineSegment(sketch, "E123", {"start": v(-48.84, 42.9) * mm, "end": v(-48.85, 42.82) * mm});
            skLineSegment(sketch, "E124", {"start": v(-48.85, 42.82) * mm, "end": v(-48.85, 42.7) * mm});
            skLineSegment(sketch, "E125", {"start": v(-48.85, 42.7) * mm, "end": v(-48.86, 42.52) * mm});
            skLineSegment(sketch, "E126", {"start": v(-48.86, 42.52) * mm, "end": v(-48.86, 42.26) * mm});
            skLineSegment(sketch, "E127", {"start": v(-48.86, 42.26) * mm, "end": v(-48.86, 41.9) * mm});
            skLineSegment(sketch, "E128", {"start": v(-48.86, 41.9) * mm, "end": v(-48.87, 41.43) * mm});
            skLineSegment(sketch, "E129", {"start": v(-48.87, 41.43) * mm, "end": v(-48.87, 39.99) * mm});
            skLineSegment(sketch, "E130", {"start": v(-48.87, 39.99) * mm, "end": v(-50.6, 39.99) * mm});
            skLineSegment(sketch, "E131", {"start": v(-50.6, 39.99) * mm, "end": v(-50.6, 42.43) * mm});
            skLineSegment(sketch, "E132", {"start": v(-50.6, 42.43) * mm, "end": v(-50.6, 42.43) * mm});
            skLineSegment(sketch, "E133", {"start": v(-43.28, 39.9) * mm, "end": v(-44.1, 40.15) * mm});
            skLineSegment(sketch, "E134", {"start": v(-44.1, 40.15) * mm, "end": v(-44.75, 40.62) * mm});
            skLineSegment(sketch, "E135", {"start": v(-44.75, 40.62) * mm, "end": v(-45.17, 41.17) * mm});
            skLineSegment(sketch, "E136", {"start": v(-45.17, 41.17) * mm, "end": v(-45.4, 41.84) * mm});
            skLineSegment(sketch, "E137", {"start": v(-45.4, 41.84) * mm, "end": v(-45.43, 41.96) * mm});
            skLineSegment(sketch, "E138", {"start": v(-45.43, 41.96) * mm, "end": v(-45.44, 42.07) * mm});
            skLineSegment(sketch, "E139", {"start": v(-45.44, 42.07) * mm, "end": v(-45.45, 42.22) * mm});
            skLineSegment(sketch, "E140", {"start": v(-45.45, 42.22) * mm, "end": v(-45.45, 42.42) * mm});
            skLineSegment(sketch, "E141", {"start": v(-45.45, 42.42) * mm, "end": v(-45.45, 42.63) * mm});
            skLineSegment(sketch, "E142", {"start": v(-45.45, 42.63) * mm, "end": v(-45.44, 42.77) * mm});
            skLineSegment(sketch, "E143", {"start": v(-45.44, 42.77) * mm, "end": v(-45.43, 42.88) * mm});
            skLineSegment(sketch, "E144", {"start": v(-45.43, 42.88) * mm, "end": v(-45.4, 43) * mm});
            skLineSegment(sketch, "E145", {"start": v(-45.4, 43) * mm, "end": v(-45.15, 43.7) * mm});
            skLineSegment(sketch, "E146", {"start": v(-45.15, 43.7) * mm, "end": v(-44.72, 44.29) * mm});
            skLineSegment(sketch, "E147", {"start": v(-44.72, 44.29) * mm, "end": v(-44.15, 44.71) * mm});
            skLineSegment(sketch, "E148", {"start": v(-44.15, 44.71) * mm, "end": v(-43.47, 44.95) * mm});
            skLineSegment(sketch, "E149", {"start": v(-43.47, 44.95) * mm, "end": v(-43.24, 44.98) * mm});
            skLineSegment(sketch, "E150", {"start": v(-43.24, 44.98) * mm, "end": v(-42.95, 44.98) * mm});
            skLineSegment(sketch, "E151", {"start": v(-42.95, 44.98) * mm, "end": v(-42.66, 44.97) * mm});
            skLineSegment(sketch, "E152", {"start": v(-42.66, 44.97) * mm, "end": v(-42.42, 44.94) * mm});
            skLineSegment(sketch, "E153", {"start": v(-42.42, 44.94) * mm, "end": v(-41.75, 44.7) * mm});
            skLineSegment(sketch, "E154", {"start": v(-41.75, 44.7) * mm, "end": v(-41.22, 44.3) * mm});
            skLineSegment(sketch, "E155", {"start": v(-41.22, 44.3) * mm, "end": v(-40.83, 43.74) * mm});
            skLineSegment(sketch, "E156", {"start": v(-40.83, 43.74) * mm, "end": v(-40.59, 43.03) * mm});
            skLineSegment(sketch, "E157", {"start": v(-40.59, 43.03) * mm, "end": v(-40.56, 42.8) * mm});
            skLineSegment(sketch, "E158", {"start": v(-40.56, 42.8) * mm, "end": v(-40.53, 42.54) * mm});
            skLineSegment(sketch, "E159", {"start": v(-40.53, 42.54) * mm, "end": v(-40.52, 42.29) * mm});
            skLineSegment(sketch, "E160", {"start": v(-40.52, 42.29) * mm, "end": v(-40.52, 42.1) * mm});
            skLineSegment(sketch, "E161", {"start": v(-40.52, 42.1) * mm, "end": v(-40.54, 41.95) * mm});
            skLineSegment(sketch, "E162", {"start": v(-40.54, 41.95) * mm, "end": v(-43.79, 41.95) * mm});
            skLineSegment(sketch, "E163", {"start": v(-43.79, 41.95) * mm, "end": v(-43.78, 41.9) * mm});
            skLineSegment(sketch, "E164", {"start": v(-43.78, 41.9) * mm, "end": v(-43.75, 41.83) * mm});
            skLineSegment(sketch, "E165", {"start": v(-43.75, 41.83) * mm, "end": v(-43.7, 41.73) * mm});
            skLineSegment(sketch, "E166", {"start": v(-43.7, 41.73) * mm, "end": v(-43.6, 41.55) * mm});
            skLineSegment(sketch, "E167", {"start": v(-43.6, 41.55) * mm, "end": v(-43.44, 41.4) * mm});
            skLineSegment(sketch, "E168", {"start": v(-43.44, 41.4) * mm, "end": v(-43.25, 41.28) * mm});
            skLineSegment(sketch, "E169", {"start": v(-43.25, 41.28) * mm, "end": v(-43.04, 41.2) * mm});
            skLineSegment(sketch, "E170", {"start": v(-43.04, 41.2) * mm, "end": v(-42.87, 41.18) * mm});
            skLineSegment(sketch, "E171", {"start": v(-42.87, 41.18) * mm, "end": v(-42.68, 41.18) * mm});
            skLineSegment(sketch, "E172", {"start": v(-42.68, 41.18) * mm, "end": v(-42.48, 41.2) * mm});
            skLineSegment(sketch, "E173", {"start": v(-42.48, 41.2) * mm, "end": v(-42.32, 41.24) * mm});
            skLineSegment(sketch, "E174", {"start": v(-42.32, 41.24) * mm, "end": v(-42.06, 41.37) * mm});
            skLineSegment(sketch, "E175", {"start": v(-42.06, 41.37) * mm, "end": v(-41.8, 41.56) * mm});
            skLineSegment(sketch, "E176", {"start": v(-41.8, 41.56) * mm, "end": v(-41.67, 41.67) * mm});
            skLineSegment(sketch, "E177", {"start": v(-41.67, 41.67) * mm, "end": v(-41.18, 41.27) * mm});
            skLineSegment(sketch, "E178", {"start": v(-41.18, 41.27) * mm, "end": v(-40.7, 40.87) * mm});
            skLineSegment(sketch, "E179", {"start": v(-40.7, 40.87) * mm, "end": v(-40.8, 40.77) * mm});
            skLineSegment(sketch, "E180", {"start": v(-40.8, 40.77) * mm, "end": v(-41.4, 40.25) * mm});
            skLineSegment(sketch, "E181", {"start": v(-41.4, 40.25) * mm, "end": v(-42.17, 39.94) * mm});
            skLineSegment(sketch, "E182", {"start": v(-42.17, 39.94) * mm, "end": v(-42.29, 39.92) * mm});
            skLineSegment(sketch, "E183", {"start": v(-42.29, 39.92) * mm, "end": v(-42.4, 39.9) * mm});
            skLineSegment(sketch, "E184", {"start": v(-42.4, 39.9) * mm, "end": v(-42.56, 39.9) * mm});
            skLineSegment(sketch, "E185", {"start": v(-42.56, 39.9) * mm, "end": v(-42.78, 39.9) * mm});
            skLineSegment(sketch, "E186", {"start": v(-42.78, 39.9) * mm, "end": v(-42.94, 39.9) * mm});
            skLineSegment(sketch, "E187", {"start": v(-42.94, 39.9) * mm, "end": v(-43.1, 39.9) * mm});
            skLineSegment(sketch, "E188", {"start": v(-43.1, 39.9) * mm, "end": v(-43.2, 39.9) * mm});
            skLineSegment(sketch, "E189", {"start": v(-43.2, 39.9) * mm, "end": v(-43.28, 39.9) * mm});
            skLineSegment(sketch, "E190", {"start": v(-43.28, 39.9) * mm, "end": v(-43.28, 39.9) * mm});
            skLineSegment(sketch, "E191", {"start": v(-42.15, 42.88) * mm, "end": v(-42.16, 42.95) * mm});
            skLineSegment(sketch, "E192", {"start": v(-42.16, 42.95) * mm, "end": v(-42.2, 43.05) * mm});
            skLineSegment(sketch, "E193", {"start": v(-42.2, 43.05) * mm, "end": v(-42.23, 43.17) * mm});
            skLineSegment(sketch, "E194", {"start": v(-42.23, 43.17) * mm, "end": v(-42.27, 43.27) * mm});
            skLineSegment(sketch, "E195", {"start": v(-42.27, 43.27) * mm, "end": v(-42.42, 43.48) * mm});
            skLineSegment(sketch, "E196", {"start": v(-42.42, 43.48) * mm, "end": v(-42.62, 43.63) * mm});
            skLineSegment(sketch, "E197", {"start": v(-42.62, 43.63) * mm, "end": v(-42.86, 43.7) * mm});
            skLineSegment(sketch, "E198", {"start": v(-42.86, 43.7) * mm, "end": v(-43.11, 43.7) * mm});
            skLineSegment(sketch, "E199", {"start": v(-43.11, 43.7) * mm, "end": v(-43.34, 43.62) * mm});
            skLineSegment(sketch, "E200", {"start": v(-43.34, 43.62) * mm, "end": v(-43.53, 43.47) * mm});
            skLineSegment(sketch, "E201", {"start": v(-43.53, 43.47) * mm, "end": v(-43.68, 43.26) * mm});
            skLineSegment(sketch, "E202", {"start": v(-43.68, 43.26) * mm, "end": v(-43.79, 43) * mm});
            skLineSegment(sketch, "E203", {"start": v(-43.79, 43) * mm, "end": v(-43.82, 42.85) * mm});
            skLineSegment(sketch, "E204", {"start": v(-43.82, 42.85) * mm, "end": v(-42.99, 42.85) * mm});
            skLineSegment(sketch, "E205", {"start": v(-42.99, 42.85) * mm, "end": v(-42.73, 42.85) * mm});
            skLineSegment(sketch, "E206", {"start": v(-42.73, 42.85) * mm, "end": v(-42.54, 42.85) * mm});
            skLineSegment(sketch, "E207", {"start": v(-42.54, 42.85) * mm, "end": v(-42.39, 42.86) * mm});
            skLineSegment(sketch, "E208", {"start": v(-42.39, 42.86) * mm, "end": v(-42.28, 42.86) * mm});
            skLineSegment(sketch, "E209", {"start": v(-42.28, 42.86) * mm, "end": v(-42.21, 42.86) * mm});
            skLineSegment(sketch, "E210", {"start": v(-42.21, 42.86) * mm, "end": v(-42.17, 42.86) * mm});
            skLineSegment(sketch, "E211", {"start": v(-42.17, 42.86) * mm, "end": v(-42.15, 42.87) * mm});
            skLineSegment(sketch, "E212", {"start": v(-42.15, 42.87) * mm, "end": v(-42.15, 42.88) * mm});
            skLineSegment(sketch, "E213", {"start": v(-42.15, 42.88) * mm, "end": v(-42.15, 42.88) * mm});
            skLineSegment(sketch, "E214", {"start": v(-40.19, 41.72) * mm, "end": v(-40.19, 44.88) * mm});
            skLineSegment(sketch, "E215", {"start": v(-40.19, 44.88) * mm, "end": v(-38.46, 44.88) * mm});
            skLineSegment(sketch, "E216", {"start": v(-38.46, 44.88) * mm, "end": v(-38.46, 44.25) * mm});
            skLineSegment(sketch, "E217", {"start": v(-38.46, 44.25) * mm, "end": v(-38.3, 44.42) * mm});
            skLineSegment(sketch, "E218", {"start": v(-38.3, 44.42) * mm, "end": v(-38.02, 44.66) * mm});
            skLineSegment(sketch, "E219", {"start": v(-38.02, 44.66) * mm, "end": v(-37.74, 44.83) * mm});
            skLineSegment(sketch, "E220", {"start": v(-37.74, 44.83) * mm, "end": v(-37.43, 44.94) * mm});
            skLineSegment(sketch, "E221", {"start": v(-37.43, 44.94) * mm, "end": v(-37.08, 44.99) * mm});
            skLineSegment(sketch, "E222", {"start": v(-37.08, 44.99) * mm, "end": v(-36.37, 44.9) * mm});
            skLineSegment(sketch, "E223", {"start": v(-36.37, 44.9) * mm, "end": v(-35.75, 44.57) * mm});
            skLineSegment(sketch, "E224", {"start": v(-35.75, 44.57) * mm, "end": v(-35.26, 44.04) * mm});
            skLineSegment(sketch, "E225", {"start": v(-35.26, 44.04) * mm, "end": v(-34.94, 43.35) * mm});
            skLineSegment(sketch, "E226", {"start": v(-34.94, 43.35) * mm, "end": v(-34.82, 42.57) * mm});
            skLineSegment(sketch, "E227", {"start": v(-34.82, 42.57) * mm, "end": v(-34.88, 41.76) * mm});
            skLineSegment(sketch, "E228", {"start": v(-34.88, 41.76) * mm, "end": v(-35.1, 41.12) * mm});
            skLineSegment(sketch, "E229", {"start": v(-35.1, 41.12) * mm, "end": v(-35.44, 40.6) * mm});
            skLineSegment(sketch, "E230", {"start": v(-35.44, 40.6) * mm, "end": v(-35.91, 40.19) * mm});
            skLineSegment(sketch, "E231", {"start": v(-35.91, 40.19) * mm, "end": v(-36.47, 39.94) * mm});
            skLineSegment(sketch, "E232", {"start": v(-36.47, 39.94) * mm, "end": v(-36.59, 39.92) * mm});
            skLineSegment(sketch, "E233", {"start": v(-36.59, 39.92) * mm, "end": v(-36.69, 39.9) * mm});
            skLineSegment(sketch, "E234", {"start": v(-36.69, 39.9) * mm, "end": v(-36.8, 39.9) * mm});
            skLineSegment(sketch, "E235", {"start": v(-36.8, 39.9) * mm, "end": v(-36.98, 39.9) * mm});
            skLineSegment(sketch, "E236", {"start": v(-36.98, 39.9) * mm, "end": v(-37.16, 39.9) * mm});
            skLineSegment(sketch, "E237", {"start": v(-37.16, 39.9) * mm, "end": v(-37.28, 39.9) * mm});
            skLineSegment(sketch, "E238", {"start": v(-37.28, 39.9) * mm, "end": v(-37.38, 39.92) * mm});
            skLineSegment(sketch, "E239", {"start": v(-37.38, 39.92) * mm, "end": v(-37.48, 39.94) * mm});
            skLineSegment(sketch, "E240", {"start": v(-37.48, 39.94) * mm, "end": v(-37.71, 40.02) * mm});
            skLineSegment(sketch, "E241", {"start": v(-37.71, 40.02) * mm, "end": v(-37.92, 40.12) * mm});
            skLineSegment(sketch, "E242", {"start": v(-37.92, 40.12) * mm, "end": v(-38.12, 40.26) * mm});
            skLineSegment(sketch, "E243", {"start": v(-38.12, 40.26) * mm, "end": v(-38.32, 40.43) * mm});
            skLineSegment(sketch, "E244", {"start": v(-38.32, 40.43) * mm, "end": v(-38.46, 40.56) * mm});
            skLineSegment(sketch, "E245", {"start": v(-38.46, 40.56) * mm, "end": v(-38.46, 38.54) * mm});
            skLineSegment(sketch, "E246", {"start": v(-38.46, 38.54) * mm, "end": v(-40.19, 38.54) * mm});
            skLineSegment(sketch, "E247", {"start": v(-40.19, 38.54) * mm, "end": v(-40.19, 41.72) * mm});
            skLineSegment(sketch, "E248", {"start": v(-40.19, 41.72) * mm, "end": v(-40.19, 41.72) * mm});
            skLineSegment(sketch, "E249", {"start": v(-37.34, 41.35) * mm, "end": v(-37.15, 41.4) * mm});
            skLineSegment(sketch, "E250", {"start": v(-37.15, 41.4) * mm, "end": v(-36.95, 41.52) * mm});
            skLineSegment(sketch, "E251", {"start": v(-36.95, 41.52) * mm, "end": v(-36.79, 41.67) * mm});
            skLineSegment(sketch, "E252", {"start": v(-36.79, 41.67) * mm, "end": v(-36.66, 41.84) * mm});
            skLineSegment(sketch, "E253", {"start": v(-36.66, 41.84) * mm, "end": v(-36.57, 42.06) * mm});
            skLineSegment(sketch, "E254", {"start": v(-36.57, 42.06) * mm, "end": v(-36.53, 42.3) * mm});
            skLineSegment(sketch, "E255", {"start": v(-36.53, 42.3) * mm, "end": v(-36.53, 42.53) * mm});
            skLineSegment(sketch, "E256", {"start": v(-36.53, 42.53) * mm, "end": v(-36.57, 42.76) * mm});
            skLineSegment(sketch, "E257", {"start": v(-36.57, 42.76) * mm, "end": v(-36.72, 43.1) * mm});
            skLineSegment(sketch, "E258", {"start": v(-36.72, 43.1) * mm, "end": v(-36.97, 43.37) * mm});
            skLineSegment(sketch, "E259", {"start": v(-36.97, 43.37) * mm, "end": v(-37.28, 43.51) * mm});
            skLineSegment(sketch, "E260", {"start": v(-37.28, 43.51) * mm, "end": v(-37.64, 43.53) * mm});
            skLineSegment(sketch, "E261", {"start": v(-37.64, 43.53) * mm, "end": v(-37.91, 43.44) * mm});
            skLineSegment(sketch, "E262", {"start": v(-37.91, 43.44) * mm, "end": v(-38.15, 43.27) * mm});
            skLineSegment(sketch, "E263", {"start": v(-38.15, 43.27) * mm, "end": v(-38.33, 43.04) * mm});
            skLineSegment(sketch, "E264", {"start": v(-38.33, 43.04) * mm, "end": v(-38.45, 42.75) * mm});
            skLineSegment(sketch, "E265", {"start": v(-38.45, 42.75) * mm, "end": v(-38.47, 42.61) * mm});
            skLineSegment(sketch, "E266", {"start": v(-38.47, 42.61) * mm, "end": v(-38.48, 42.44) * mm});
            skLineSegment(sketch, "E267", {"start": v(-38.48, 42.44) * mm, "end": v(-38.47, 42.27) * mm});
            skLineSegment(sketch, "E268", {"start": v(-38.47, 42.27) * mm, "end": v(-38.45, 42.13) * mm});
            skLineSegment(sketch, "E269", {"start": v(-38.45, 42.13) * mm, "end": v(-38.34, 41.85) * mm});
            skLineSegment(sketch, "E270", {"start": v(-38.34, 41.85) * mm, "end": v(-38.17, 41.62) * mm});
            skLineSegment(sketch, "E271", {"start": v(-38.17, 41.62) * mm, "end": v(-37.95, 41.45) * mm});
            skLineSegment(sketch, "E272", {"start": v(-37.95, 41.45) * mm, "end": v(-37.7, 41.35) * mm});
            skLineSegment(sketch, "E273", {"start": v(-37.7, 41.35) * mm, "end": v(-37.53, 41.33) * mm});
            skLineSegment(sketch, "E274", {"start": v(-37.53, 41.33) * mm, "end": v(-37.34, 41.35) * mm});
            skLineSegment(sketch, "E275", {"start": v(-28.9, 42.44) * mm, "end": v(-28.9, 44.88) * mm});
            skLineSegment(sketch, "E276", {"start": v(-28.9, 44.88) * mm, "end": v(-27.16, 44.88) * mm});
            skLineSegment(sketch, "E277", {"start": v(-27.16, 44.88) * mm, "end": v(-27.16, 40) * mm});
            skLineSegment(sketch, "E278", {"start": v(-27.16, 40) * mm, "end": v(-28.9, 40) * mm});
            skLineSegment(sketch, "E279", {"start": v(-28.9, 40) * mm, "end": v(-28.9, 42.44) * mm});
            skLineSegment(sketch, "E280", {"start": v(-32.41, 39.93) * mm, "end": v(-33.2, 40.17) * mm});
            skLineSegment(sketch, "E281", {"start": v(-33.2, 40.17) * mm, "end": v(-33.84, 40.6) * mm});
            skLineSegment(sketch, "E282", {"start": v(-33.84, 40.6) * mm, "end": v(-34.31, 41.2) * mm});
            skLineSegment(sketch, "E283", {"start": v(-34.31, 41.2) * mm, "end": v(-34.6, 41.94) * mm});
            skLineSegment(sketch, "E284", {"start": v(-34.6, 41.94) * mm, "end": v(-34.63, 42.13) * mm});
            skLineSegment(sketch, "E285", {"start": v(-34.63, 42.13) * mm, "end": v(-34.64, 42.37) * mm});
            skLineSegment(sketch, "E286", {"start": v(-34.64, 42.37) * mm, "end": v(-34.64, 42.62) * mm});
            skLineSegment(sketch, "E287", {"start": v(-34.65, 42.42) * mm, "end": v(-34.64, 42.62) * mm});
            skLineSegment(sketch, "E288", {"start": v(-34.62, 42.83) * mm, "end": v(-34.36, 43.6) * mm});
            skLineSegment(sketch, "E289", {"start": v(-34.36, 43.6) * mm, "end": v(-33.86, 44.26) * mm});
            skLineSegment(sketch, "E290", {"start": v(-33.86, 44.26) * mm, "end": v(-33.48, 44.57) * mm});
            skLineSegment(sketch, "E291", {"start": v(-33.48, 44.57) * mm, "end": v(-33.05, 44.8) * mm});
            skLineSegment(sketch, "E292", {"start": v(-33.05, 44.8) * mm, "end": v(-32.58, 44.94) * mm});
            skLineSegment(sketch, "E293", {"start": v(-32.58, 44.94) * mm, "end": v(-32.07, 45) * mm});
            skLineSegment(sketch, "E294", {"start": v(-32.07, 45) * mm, "end": v(-31.49, 44.98) * mm});
            skLineSegment(sketch, "E295", {"start": v(-31.49, 44.98) * mm, "end": v(-30.94, 44.84) * mm});
            skLineSegment(sketch, "E296", {"start": v(-30.94, 44.84) * mm, "end": v(-30.44, 44.6) * mm});
            skLineSegment(sketch, "E297", {"start": v(-30.44, 44.6) * mm, "end": v(-30, 44.26) * mm});
            skLineSegment(sketch, "E298", {"start": v(-30, 44.26) * mm, "end": v(-29.53, 43.63) * mm});
            skLineSegment(sketch, "E299", {"start": v(-29.53, 43.63) * mm, "end": v(-29.27, 42.9) * mm});
            skLineSegment(sketch, "E300", {"start": v(-29.27, 42.9) * mm, "end": v(-29.25, 42.7) * mm});
            skLineSegment(sketch, "E301", {"start": v(-29.25, 42.7) * mm, "end": v(-29.24, 42.45) * mm});
            skLineSegment(sketch, "E302", {"start": v(-29.24, 42.45) * mm, "end": v(-29.26, 42.2) * mm});
            skLineSegment(sketch, "E303", {"start": v(-29.26, 42.2) * mm, "end": v(-29.29, 42) * mm});
            skLineSegment(sketch, "E304", {"start": v(-29.29, 42) * mm, "end": v(-29.55, 41.25) * mm});
            skLineSegment(sketch, "E305", {"start": v(-29.55, 41.25) * mm, "end": v(-30.03, 40.64) * mm});
            skLineSegment(sketch, "E306", {"start": v(-30.03, 40.64) * mm, "end": v(-30.67, 40.19) * mm});
            skLineSegment(sketch, "E307", {"start": v(-30.67, 40.19) * mm, "end": v(-31.44, 39.94) * mm});
            skLineSegment(sketch, "E308", {"start": v(-31.44, 39.94) * mm, "end": v(-31.93, 39.9) * mm});
            skLineSegment(sketch, "E309", {"start": v(-31.93, 39.9) * mm, "end": v(-32.41, 39.93) * mm});
            skLineSegment(sketch, "E310", {"start": v(-31.68, 41.4) * mm, "end": v(-31.45, 41.5) * mm});
            skLineSegment(sketch, "E311", {"start": v(-31.45, 41.5) * mm, "end": v(-31.26, 41.63) * mm});
            skLineSegment(sketch, "E312", {"start": v(-31.26, 41.63) * mm, "end": v(-31.1, 41.82) * mm});
            skLineSegment(sketch, "E313", {"start": v(-31.1, 41.82) * mm, "end": v(-31, 42.06) * mm});
            skLineSegment(sketch, "E314", {"start": v(-31, 42.06) * mm, "end": v(-30.93, 42.42) * mm});
            skLineSegment(sketch, "E315", {"start": v(-30.93, 42.42) * mm, "end": v(-30.97, 42.77) * mm});
            skLineSegment(sketch, "E316", {"start": v(-30.97, 42.77) * mm, "end": v(-31.1, 43.04) * mm});
            skLineSegment(sketch, "E317", {"start": v(-31.1, 43.04) * mm, "end": v(-31.27, 43.26) * mm});
            skLineSegment(sketch, "E318", {"start": v(-31.27, 43.26) * mm, "end": v(-31.5, 43.42) * mm});
            skLineSegment(sketch, "E319", {"start": v(-31.5, 43.42) * mm, "end": v(-31.76, 43.52) * mm});
            skLineSegment(sketch, "E320", {"start": v(-31.76, 43.52) * mm, "end": v(-31.87, 43.54) * mm});
            skLineSegment(sketch, "E321", {"start": v(-31.87, 43.54) * mm, "end": v(-31.96, 43.55) * mm});
            skLineSegment(sketch, "E322", {"start": v(-31.96, 43.55) * mm, "end": v(-32.18, 43.52) * mm});
            skLineSegment(sketch, "E323", {"start": v(-32.18, 43.52) * mm, "end": v(-32.4, 43.44) * mm});
            skLineSegment(sketch, "E324", {"start": v(-32.4, 43.44) * mm, "end": v(-32.58, 43.32) * mm});
            skLineSegment(sketch, "E325", {"start": v(-32.58, 43.32) * mm, "end": v(-32.73, 43.16) * mm});
            skLineSegment(sketch, "E326", {"start": v(-32.73, 43.16) * mm, "end": v(-32.85, 42.97) * mm});
            skLineSegment(sketch, "E327", {"start": v(-32.85, 42.97) * mm, "end": v(-32.92, 42.76) * mm});
            skLineSegment(sketch, "E328", {"start": v(-32.92, 42.76) * mm, "end": v(-32.95, 42.62) * mm});
            skLineSegment(sketch, "E329", {"start": v(-32.95, 42.62) * mm, "end": v(-32.95, 42.46) * mm});
            skLineSegment(sketch, "E330", {"start": v(-32.95, 42.46) * mm, "end": v(-32.95, 42.3) * mm});
            skLineSegment(sketch, "E331", {"start": v(-32.95, 42.3) * mm, "end": v(-32.92, 42.18) * mm});
            skLineSegment(sketch, "E332", {"start": v(-32.92, 42.18) * mm, "end": v(-32.82, 41.9) * mm});
            skLineSegment(sketch, "E333", {"start": v(-32.82, 41.9) * mm, "end": v(-32.65, 41.68) * mm});
            skLineSegment(sketch, "E334", {"start": v(-32.65, 41.68) * mm, "end": v(-32.44, 41.5) * mm});
            skLineSegment(sketch, "E335", {"start": v(-32.44, 41.5) * mm, "end": v(-32.19, 41.4) * mm});
            skLineSegment(sketch, "E336", {"start": v(-32.19, 41.4) * mm, "end": v(-31.94, 41.37) * mm});
            skLineSegment(sketch, "E337", {"start": v(-31.94, 41.37) * mm, "end": v(-31.68, 41.4) * mm});
            skLineSegment(sketch, "E338", {"start": v(-31.68, 41.4) * mm, "end": v(-31.68, 41.4) * mm});
            skLineSegment(sketch, "E339", {"start": v(-26.6, 42.44) * mm, "end": v(-26.6, 44.88) * mm});
            skLineSegment(sketch, "E340", {"start": v(-26.6, 44.88) * mm, "end": v(-24.86, 44.88) * mm});
            skLineSegment(sketch, "E341", {"start": v(-24.86, 44.88) * mm, "end": v(-24.86, 44.23) * mm});
            skLineSegment(sketch, "E342", {"start": v(-24.86, 44.23) * mm, "end": v(-24.68, 44.41) * mm});
            skLineSegment(sketch, "E343", {"start": v(-24.68, 44.41) * mm, "end": v(-24.33, 44.71) * mm});
            skLineSegment(sketch, "E344", {"start": v(-24.33, 44.71) * mm, "end": v(-23.96, 44.9) * mm});
            skLineSegment(sketch, "E345", {"start": v(-23.96, 44.9) * mm, "end": v(-23.55, 45) * mm});
            skLineSegment(sketch, "E346", {"start": v(-23.55, 45) * mm, "end": v(-23.12, 44.97) * mm});
            skLineSegment(sketch, "E347", {"start": v(-23.12, 44.97) * mm, "end": v(-22.6, 44.82) * mm});
            skLineSegment(sketch, "E348", {"start": v(-22.6, 44.82) * mm, "end": v(-22.2, 44.52) * mm});
            skLineSegment(sketch, "E349", {"start": v(-22.2, 44.52) * mm, "end": v(-21.91, 44.08) * mm});
            skLineSegment(sketch, "E350", {"start": v(-21.91, 44.08) * mm, "end": v(-21.76, 43.53) * mm});
            skLineSegment(sketch, "E351", {"start": v(-21.76, 43.53) * mm, "end": v(-21.76, 43.35) * mm});
            skLineSegment(sketch, "E352", {"start": v(-21.76, 43.35) * mm, "end": v(-21.75, 42.95) * mm});
            skLineSegment(sketch, "E353", {"start": v(-21.75, 42.95) * mm, "end": v(-21.74, 42.39) * mm});
            skLineSegment(sketch, "E354", {"start": v(-21.74, 42.39) * mm, "end": v(-21.74, 41.7) * mm});
            skLineSegment(sketch, "E355", {"start": v(-21.74, 41.7) * mm, "end": v(-21.74, 40) * mm});
            skLineSegment(sketch, "E356", {"start": v(-21.74, 40) * mm, "end": v(-23.47, 40) * mm});
            skLineSegment(sketch, "E357", {"start": v(-23.47, 40) * mm, "end": v(-23.47, 41.39) * mm});
            skLineSegment(sketch, "E358", {"start": v(-23.47, 41.39) * mm, "end": v(-23.47, 41.89) * mm});
            skLineSegment(sketch, "E359", {"start": v(-23.47, 41.89) * mm, "end": v(-23.47, 42.27) * mm});
            skLineSegment(sketch, "E360", {"start": v(-23.47, 42.27) * mm, "end": v(-23.48, 42.55) * mm});
            skLineSegment(sketch, "E361", {"start": v(-23.48, 42.55) * mm, "end": v(-23.49, 42.75) * mm});
            skLineSegment(sketch, "E362", {"start": v(-23.49, 42.75) * mm, "end": v(-23.5, 42.89) * mm});
            skLineSegment(sketch, "E363", {"start": v(-23.5, 42.89) * mm, "end": v(-23.52, 42.98) * mm});
            skLineSegment(sketch, "E364", {"start": v(-23.52, 42.98) * mm, "end": v(-23.54, 43.05) * mm});
            skLineSegment(sketch, "E365", {"start": v(-23.54, 43.05) * mm, "end": v(-23.58, 43.12) * mm});
            skLineSegment(sketch, "E366", {"start": v(-23.58, 43.12) * mm, "end": v(-23.73, 43.31) * mm});
            skLineSegment(sketch, "E367", {"start": v(-23.73, 43.31) * mm, "end": v(-23.95, 43.43) * mm});
            skLineSegment(sketch, "E368", {"start": v(-23.95, 43.43) * mm, "end": v(-24.2, 43.46) * mm});
            skLineSegment(sketch, "E369", {"start": v(-24.2, 43.46) * mm, "end": v(-24.45, 43.4) * mm});
            skLineSegment(sketch, "E370", {"start": v(-24.45, 43.4) * mm, "end": v(-24.63, 43.26) * mm});
            skLineSegment(sketch, "E371", {"start": v(-24.63, 43.26) * mm, "end": v(-24.77, 43.07) * mm});
            skLineSegment(sketch, "E372", {"start": v(-24.77, 43.07) * mm, "end": v(-24.8, 43) * mm});
            skLineSegment(sketch, "E373", {"start": v(-24.8, 43) * mm, "end": v(-24.82, 42.93) * mm});
            skLineSegment(sketch, "E374", {"start": v(-24.82, 42.93) * mm, "end": v(-24.84, 42.83) * mm});
            skLineSegment(sketch, "E375", {"start": v(-24.84, 42.83) * mm, "end": v(-24.85, 42.7) * mm});
            skLineSegment(sketch, "E376", {"start": v(-24.85, 42.7) * mm, "end": v(-24.86, 42.5) * mm});
            skLineSegment(sketch, "E377", {"start": v(-24.86, 42.5) * mm, "end": v(-24.86, 42.22) * mm});
            skLineSegment(sketch, "E378", {"start": v(-24.86, 42.22) * mm, "end": v(-24.86, 41.85) * mm});
            skLineSegment(sketch, "E379", {"start": v(-24.86, 41.85) * mm, "end": v(-24.86, 41.36) * mm});
            skLineSegment(sketch, "E380", {"start": v(-24.86, 41.36) * mm, "end": v(-24.86, 40) * mm});
            skLineSegment(sketch, "E381", {"start": v(-24.86, 40) * mm, "end": v(-26.6, 40) * mm});
            skLineSegment(sketch, "E382", {"start": v(-26.6, 40) * mm, "end": v(-26.6, 42.44) * mm});
            skLineSegment(sketch, "E383", {"start": v(-26.6, 42.44) * mm, "end": v(-26.6, 42.44) * mm});
            skLineSegment(sketch, "E384", {"start": v(-20.9, 41.78) * mm, "end": v(-20.9, 43.53) * mm});
            skLineSegment(sketch, "E385", {"start": v(-20.9, 43.53) * mm, "end": v(-21.49, 43.53) * mm});
            skLineSegment(sketch, "E386", {"start": v(-21.49, 43.53) * mm, "end": v(-21.49, 44.92) * mm});
            skLineSegment(sketch, "E387", {"start": v(-21.49, 44.92) * mm, "end": v(-20.9, 44.92) * mm});
            skLineSegment(sketch, "E388", {"start": v(-20.9, 44.92) * mm, "end": v(-20.9, 46.16) * mm});
            skLineSegment(sketch, "E389", {"start": v(-20.9, 46.16) * mm, "end": v(-19.17, 46.16) * mm});
            skLineSegment(sketch, "E390", {"start": v(-19.17, 46.16) * mm, "end": v(-19.17, 44.92) * mm});
            skLineSegment(sketch, "E391", {"start": v(-19.17, 44.92) * mm, "end": v(-18.05, 44.92) * mm});
            skLineSegment(sketch, "E392", {"start": v(-18.05, 44.92) * mm, "end": v(-18.05, 43.53) * mm});
            skLineSegment(sketch, "E393", {"start": v(-18.05, 43.53) * mm, "end": v(-19.17, 43.53) * mm});
            skLineSegment(sketch, "E394", {"start": v(-19.17, 43.53) * mm, "end": v(-19.17, 40.03) * mm});
            skLineSegment(sketch, "E395", {"start": v(-19.17, 40.03) * mm, "end": v(-20.9, 40.03) * mm});
            skLineSegment(sketch, "E396", {"start": v(-20.9, 40.03) * mm, "end": v(-20.9, 41.78) * mm});
            skLineSegment(sketch, "E397", {"start": v(-17.67, 40.02) * mm, "end": v(-17.94, 40.14) * mm});
            skLineSegment(sketch, "E398", {"start": v(-17.94, 40.14) * mm, "end": v(-18.17, 40.33) * mm});
            skLineSegment(sketch, "E399", {"start": v(-18.17, 40.33) * mm, "end": v(-18.34, 40.56) * mm});
            skLineSegment(sketch, "E400", {"start": v(-18.34, 40.56) * mm, "end": v(-18.44, 40.84) * mm});
            skLineSegment(sketch, "E401", {"start": v(-18.44, 40.84) * mm, "end": v(-18.45, 40.97) * mm});
            skLineSegment(sketch, "E402", {"start": v(-18.45, 40.97) * mm, "end": v(-18.45, 41.13) * mm});
            skLineSegment(sketch, "E403", {"start": v(-18.45, 41.13) * mm, "end": v(-18.43, 41.27) * mm});
            skLineSegment(sketch, "E404", {"start": v(-18.43, 41.27) * mm, "end": v(-18.4, 41.4) * mm});
            skLineSegment(sketch, "E405", {"start": v(-18.4, 41.4) * mm, "end": v(-18.28, 41.62) * mm});
            skLineSegment(sketch, "E406", {"start": v(-18.28, 41.62) * mm, "end": v(-18.13, 41.8) * mm});
            skLineSegment(sketch, "E407", {"start": v(-18.13, 41.8) * mm, "end": v(-17.93, 41.96) * mm});
            skLineSegment(sketch, "E408", {"start": v(-17.93, 41.96) * mm, "end": v(-17.7, 42.06) * mm});
            skLineSegment(sketch, "E409", {"start": v(-17.7, 42.06) * mm, "end": v(-17.56, 42.09) * mm});
            skLineSegment(sketch, "E410", {"start": v(-17.56, 42.09) * mm, "end": v(-17.4, 42.1) * mm});
            skLineSegment(sketch, "E411", {"start": v(-17.4, 42.1) * mm, "end": v(-17.23, 42.09) * mm});
            skLineSegment(sketch, "E412", {"start": v(-17.23, 42.09) * mm, "end": v(-17.1, 42.06) * mm});
            skLineSegment(sketch, "E413", {"start": v(-17.1, 42.06) * mm, "end": v(-16.78, 41.9) * mm});
            skLineSegment(sketch, "E414", {"start": v(-16.78, 41.9) * mm, "end": v(-16.54, 41.67) * mm});
            skLineSegment(sketch, "E415", {"start": v(-16.54, 41.67) * mm, "end": v(-16.4, 41.38) * mm});
            skLineSegment(sketch, "E416", {"start": v(-16.4, 41.38) * mm, "end": v(-16.35, 41.07) * mm});
            skLineSegment(sketch, "E417", {"start": v(-16.4, 40.7) * mm, "end": v(-16.56, 40.4) * mm});
            skLineSegment(sketch, "E418", {"start": v(-16.56, 40.4) * mm, "end": v(-16.81, 40.16) * mm});
            skLineSegment(sketch, "E419", {"start": v(-16.81, 40.16) * mm, "end": v(-17.12, 40.02) * mm});
            skLineSegment(sketch, "E420", {"start": v(-17.12, 40.02) * mm, "end": v(-17.25, 40) * mm});
            skLineSegment(sketch, "E421", {"start": v(-17.25, 40) * mm, "end": v(-17.4, 40) * mm});
            skLineSegment(sketch, "E422", {"start": v(-17.4, 40) * mm, "end": v(-17.55, 40) * mm});
            skLineSegment(sketch, "E423", {"start": v(-17.55, 40) * mm, "end": v(-17.67, 40.02) * mm});
            skLineSegment(sketch, "E424", {"start": v(-17.67, 40.02) * mm, "end": v(-17.67, 40.02) * mm});
            skLineSegment(sketch, "E425", {"start": v(-56.34, 42.62) * mm, "end": v(-56.34, 42.37) * mm});
            skLineSegment(sketch, "E426", {"start": v(-16.35, 41.07) * mm, "end": v(-16.35, 40.88) * mm});
            skLineSegment(sketch, "E427", {"start": v(-16.35, 40.88) * mm, "end": v(-16.4, 40.7) * mm});
            skPoint(sketch, "E428.middle", {"position": v(-36.38, 42.42) * mm});
            skLineSegment(sketch, "E429", {"start": v(-34.62, 42.83) * mm, "end": v(-34.64, 42.62) * mm});
            skSolve(sketch);
        }
        {
            var Q0;
            Q0 = qSketchRegion(id + "F15", true);
            extrude(context, id + "F16", {"entities" : qUnion([Q0]), "operationType" : NewBodyOperationType.ADD, "depth" : 1 * mm});
        }
        {
            var Q0;
            Q0=qCreatedBy(id+"F14.planeOp",FACE);
            cPlane(context, id + "F17", {"entities" : qUnion([Q0]), "cplaneType" : CPlaneType.OFFSET, "offset" : 7 * mm, "oppositeDirection" : true, "width" : 150 * mm, "height" : 150 * mm});
        }
        {
            var Q0;
            Q0=makeQuery(id+"F4.imprint","IMPRINT",FACE,{"disambiguationData":[TD([[makeQuery(id+"F4.imprint","IMPRINT",EDGE,{"derivedFrom":sQuery(id+"F4.wireOp",EDGE,"E15")}),1.0]])]});
            var Q1;
            Q1=sQuery(id+"F4.wireOp",EDGE,"E15");
            var Q2;
            {var subQ0=sQuery(id+"F0.wireOp",EDGE,"E6");Q2=makeQuery(id+"F1.opExtrude","SWEPT_FACE",FACE,{"disambiguationData":[OSD([subQ0]),TDD([makeQuery(id+"F0.imprint","IMPRINT",EDGE,{"disambiguationData":[TD([[makeQuery(id+"F0.imprint","INTERSECT",VERTEX,{"derivedFrom":[subQ0,sQuery(id+"F0.wireOp",EDGE,"E8")]}),1.0]])],"derivedFrom":subQ0})])]});}
            extrude(context, id + "F18", {"entities" : qUnion([Q0]), "operationType" : NewBodyOperationType.REMOVE, "surfaceEntities" : qUnion([Q1]), "endBound" : BoundingType.UP_TO_SURFACE, "endBoundEntityFace" : qUnion([Q2]), "depth" : 25 * mm});
        }
        {
            var Q0;
            Q0=makeQuery(id+"F18.boolean.opBoolean","COPY",EDGE,{"derivedFrom":makeQuery(id+"F18.opExtrude","CAP_EDGE",EDGE,{"disambiguationData":[OSD([sQuery(id+"F4.wireOp",EDGE,"E15")])],"isStart":false})});
            var Q1;
            Q1=makeQuery(id+"F18.boolean.opBoolean","INTERSECT",EDGE,{"derivedFrom":[makeQuery(id+"F1.opExtrude","SWEPT_FACE",FACE,{"disambiguationData":[OSD([sQuery(id+"F0.wireOp",EDGE,"E7")])]}),makeQuery(id+"F18.opExtrude","SWEPT_FACE",FACE,{"disambiguationData":[OSD([sQuery(id+"F4.wireOp",EDGE,"E15")])]})]});
            var Q2;
            Q2=makeQuery(id+"F8.boolean.opBoolean","COPY",EDGE,{"derivedFrom":makeQuery(id+"F8.opExtrude","TWEAK_EDGE",EDGE,{"derivedFrom":[makeQuery(id+"F1.opExtrude","SWEPT_FACE",FACE,{"disambiguationData":[OSD([sQuery(id+"F0.wireOp",EDGE,"E11")])]}),makeQuery(id+"F7.imprint","IMPRINT",EDGE,{"derivedFrom":sQuery(id+"F7.wireOp",EDGE,"E18.0.3.0")})]})});
            var Q3;
            Q3=makeQuery(id+"F5.boolean.opBoolean","COPY",EDGE,{"derivedFrom":makeQuery(id+"F5.opExtrude","CAP_EDGE",EDGE,{"disambiguationData":[OSD([sQuery(id+"F4.wireOp",EDGE,"E16.0.1.0")])],"isStart":false})});
            var Q4;
            Q4=makeQuery(id+"F12.boolean.opBoolean","INTERSECT",EDGE,{"derivedFrom":[makeQuery(id+"F1.opExtrude","SWEPT_FACE",FACE,{"disambiguationData":[OSD([sQuery(id+"F0.wireOp",EDGE,"E2")])]}),makeQuery(id+"F12.opExtrude","SWEPT_FACE",FACE,{"disambiguationData":[OSD([sQuery(id+"F11.wireOp",EDGE,"E19")])]})]});
            var Q5;
            Q5=makeQuery(id+"F12.boolean.opBoolean","INTERSECT",EDGE,{"derivedFrom":[makeQuery(id+"F1.opExtrude","SWEPT_FACE",FACE,{"disambiguationData":[OSD([sQuery(id+"F0.wireOp",EDGE,"E7")])]}),makeQuery(id+"F12.opExtrude","SWEPT_FACE",FACE,{"disambiguationData":[OSD([sQuery(id+"F11.wireOp",EDGE,"E19")])]})]});
            fillet(context, id + "F19", {"entities" : qUnion([Q0, Q1, Q2, Q3, Q4, Q5]), "radius" : 0.5 * mm, "tangentPropagation" : true, "allowEdgeOverflow" : false});
        }
        {
            var Q0;
            Q0=makeQuery(id+"F1.opExtrude","SWEPT_FACE",FACE,{"disambiguationData":[OSD([sQuery(id+"F0.wireOp",EDGE,"E4")])]});
            var sketch = newSketch(context, id + "F20", { "sketchPlane" : qUnion([Q0])});
            skText(sketch, "E430", { "text": "gop-labs.github.io", "fontName": "OpenSans-Bold.ttf"});
            const initialGuessF20  = {"E430": [0.005, 0.053, 1, 0, 0.00483]};
            skSetInitialGuess(sketch, initialGuessF20);
            skSolve(sketch);
        }
        {
            var Q0;
            Q0 = qSketchRegion(id + "F20", true);
            extrude(context, id + "F21", {"entities" : qUnion([Q0]), "operationType" : NewBodyOperationType.REMOVE, "oppositeDirection" : true, "depth" : 0.5 * mm});
        }
        {
            var Q0;
            {var subQ0=sQuery(id+"F2.wireOp",EDGE,"E13");var subQ1=sQuery(id+"F0.wireOp",EDGE,"E3");var subQ2=sQuery(id+"F0.wireOp",EDGE,"E7");Q0=makeQuery(id+"F3.boolean.opBoolean","SPLIT",EDGE,{"disambiguationData":[TD([makeQuery(id+"F1.opExtrude","CAP_FACE",FACE,{"disambiguationData":[OSD([sQuery(id+"F0.wireOp",EDGE,"E0"),sQuery(id+"F0.wireOp",EDGE,"E1"),sQuery(id+"F0.wireOp",EDGE,"E2"),subQ1,sQuery(id+"F0.wireOp",EDGE,"E4"),sQuery(id+"F0.wireOp",EDGE,"E5"),sQuery(id+"F0.wireOp",EDGE,"E6"),subQ2,sQuery(id+"F0.wireOp",EDGE,"E8"),sQuery(id+"F0.wireOp",EDGE,"E9"),sQuery(id+"F0.wireOp",EDGE,"E11"),sQuery(id+"F0.wireOp",EDGE,"E12")])],"isStart":false}),makeQuery(id+"F1.opExtrude","SWEPT_FACE",FACE,{"disambiguationData":[OSD([subQ1])]}),makeQuery(id+"F1.opExtrude","SWEPT_FACE",FACE,{"disambiguationData":[OSD([subQ2])]}),makeQuery(id+"F3.opExtrude","SWEPT_FACE",FACE,{"disambiguationData":[OSD([subQ0])]}),makeQuery(id+"F3.opExtrude","CAP_FACE",FACE,{"disambiguationData":[OSD([subQ0])],"isStart":true})])],"derivedFrom":makeQuery(id+"F1.opExtrude","SWEPT_EDGE",EDGE,{"disambiguationData":[OSD([subQ1,subQ2])]})});}
            cPlane(context, id + "F22", {"entities" : qUnion([Q0]), "cplaneType" : CPlaneType.LINE_ANGLE, "offset" : 25 * mm, "angle" : 255 * degree, "width" : 150 * mm, "height" : 150 * mm});
        }
        {
            var Q0;
            Q0=qCreatedBy(id+"F22.planeOp",FACE);
            var sketch = newSketch(context, id + "F23", { "sketchPlane" : qUnion([Q0])});
            skText(sketch, "E431", { "text": "FLV - v0.6", "fontName": "OpenSans-Bold.ttf"});
            const initialGuessF23  = {"E431": [0.007, -0.01852, 1, 0, 0.0087]};
            skSetInitialGuess(sketch, initialGuessF23);
            skSolve(sketch);
        }
        {
            var Q0;
            Q0 = qSketchRegion(id + "F23", true);
            extrude(context, id + "F24", {"entities" : qUnion([Q0]), "operationType" : NewBodyOperationType.REMOVE, "oppositeDirection" : true, "depth" : 1.3 * mm});
        }
        {
            var Q0;
            Q0=makeQuery(id+"F12.boolean.opBoolean","COPY",FACE,{"derivedFrom":makeQuery(id+"F12.opExtrude","SWEPT_FACE",FACE,{"disambiguationData":[OSD([sQuery(id+"F11.wireOp",EDGE,"E20.right")])]})});
            cPlane(context, id + "F25", {"entities" : qUnion([Q0]), "cplaneType" : CPlaneType.OFFSET, "offset" : 0 * mm, "width" : 150 * mm, "height" : 150 * mm});
        }
        {
            var Q0;
            Q0=qCreatedBy(id+"F25.planeOp",FACE);
            var sketch = newSketch(context, id + "F26", { "sketchPlane" : qUnion([Q0])});
            skCircle(sketch, "E432", {"center": v(-11.91, 52.48) * mm, "radius": 0.4 * mm});
            skCircle(sketch, "E433", {"center": v(-13.19, 52.75) * mm, "radius": 0.37 * mm});
            skCircle(sketch, "E434", {"center": v(-12.69, 53.9) * mm, "radius": 0.32 * mm});
            skCircle(sketch, "E435", {"center": v(-11.49, 53.57) * mm, "radius": 0.3 * mm});
            skSolve(sketch);
        }
        {
            var Q0;
            Q0 = qSketchRegion(id + "F26", true);
            extrude(context, id + "F27", {"entities" : qUnion([Q0]), "operationType" : NewBodyOperationType.ADD, "depth" : 0.5 * mm, "offsetDistance" : 25 * mm});
        }
        {
            var Q0;
            Q0=makeQuery(id+"F27.opExtrude","CAP_EDGE",EDGE,{"disambiguationData":[OSD([sQuery(id+"F26.wireOp",EDGE,"E435")])],"isStart":false});
            var Q1;
            Q1=makeQuery(id+"F27.opExtrude","CAP_EDGE",EDGE,{"disambiguationData":[OSD([sQuery(id+"F26.wireOp",EDGE,"E432")])],"isStart":false});
            var Q2;
            Q2=makeQuery(id+"F27.opExtrude","CAP_EDGE",EDGE,{"disambiguationData":[OSD([sQuery(id+"F26.wireOp",EDGE,"E433")])],"isStart":false});
            var Q3;
            Q3=makeQuery(id+"F27.opExtrude","CAP_EDGE",EDGE,{"disambiguationData":[OSD([sQuery(id+"F26.wireOp",EDGE,"E434")])],"isStart":false});
            fillet(context, id + "F28", {"entities" : qUnion([Q0, Q1, Q2, Q3]), "radius" : 0.25 * mm, "tangentPropagation" : true, "allowEdgeOverflow" : false});
        }
        {
            var Q0;
            Q0=qCreatedBy(makeId("Right.planeOp"),FACE);
            var sketch = newSketch(context, id + "F29", { "sketchPlane" : qUnion([Q0])});
            skLineSegment(sketch, "E436.bottom", {"start": v(-65.41, 22.22) * mm, "end": v(-49.4, 22.22) * mm});
            skLineSegment(sketch, "E436.top", {"start": v(-65.41, 20.34) * mm, "end": v(-49.4, 20.34) * mm});
            skLineSegment(sketch, "E436.left", {"start": v(-65.41, 22.22) * mm, "end": v(-65.41, 20.34) * mm});
            skLineSegment(sketch, "E436.right", {"start": v(-49.4, 22.22) * mm, "end": v(-49.4, 20.34) * mm});
            skLineSegment(sketch, "E437", {"start": v(-65.41, 22.22) * mm, "end": v(-63.29, 25.98) * mm});
            skLineSegment(sketch, "E438", {"start": v(-63.29, 25.98) * mm, "end": v(-62.04, 24.04) * mm});
            skLineSegment(sketch, "E439", {"start": v(-62.04, 24.04) * mm, "end": v(-49.4, 22.22) * mm});
            skLineSegment(sketch, "E440", {"start": v(42.61, 20.5) * mm, "end": v(46.23, 21.26) * mm});
            skLineSegment(sketch, "E441", {"start": v(46.23, 21.26) * mm, "end": v(47.86, 23.1) * mm});
            skLineSegment(sketch, "E442", {"start": v(47.86, 23.1) * mm, "end": v(47.86, 25.13) * mm});
            skLineSegment(sketch, "E443", {"start": v(47.86, 25.13) * mm, "end": v(46.23, 25.13) * mm});
            skLineSegment(sketch, "E444", {"start": v(46.23, 25.13) * mm, "end": v(41.8, 22.13) * mm});
            skLineSegment(sketch, "E445", {"start": v(41.8, 22.13) * mm, "end": v(42.61, 20.5) * mm});
            skSolve(sketch);
        }
        {
            var Q0;
            Q0 = qSketchRegion(id + "F29", true);
            var Q1;
            Q1=makeQuery(id+"F1.opExtrude","CAP_FACE",FACE,{"disambiguationData":[OSD([sQuery(id+"F0.wireOp",EDGE,"E0"),sQuery(id+"F0.wireOp",EDGE,"E1"),sQuery(id+"F0.wireOp",EDGE,"E2"),sQuery(id+"F0.wireOp",EDGE,"E3"),sQuery(id+"F0.wireOp",EDGE,"E4"),sQuery(id+"F0.wireOp",EDGE,"E5"),sQuery(id+"F0.wireOp",EDGE,"E6"),sQuery(id+"F0.wireOp",EDGE,"E7"),sQuery(id+"F0.wireOp",EDGE,"E8"),sQuery(id+"F0.wireOp",EDGE,"E9"),sQuery(id+"F0.wireOp",EDGE,"E11"),sQuery(id+"F0.wireOp",EDGE,"E12")])],"isStart":false});
            extrude(context, id + "F30", {"entities" : qUnion([Q0]), "operationType" : NewBodyOperationType.ADD, "endBound" : BoundingType.UP_TO_SURFACE, "depth" : 25 * mm, "endBoundEntityFace" : qUnion([Q1]), "offsetDistance" : 25 * mm});
        }
        {
            var Q0;
            Q0=qCreatedBy(makeId("Top.planeOp"),FACE);
            var sketch = newSketch(context, id + "F31", { "sketchPlane" : qUnion([Q0])});
            skEllipse(sketch, "E446", {"center": v(34.65, -57.08) * mm, "majorRadius": 31.68 * mm, "minorRadius": 3.4 * mm, "majorAxis": v(1, 0)});
            skSolve(sketch);
        }
        {
            var Q0;
            Q0 = qSketchRegion(id + "F31", true);
            var Q1;
            Q1=makeQuery(id+"F30.opExtrude","SWEPT_FACE",FACE,{"disambiguationData":[OSD([sQuery(id+"F29.wireOp",EDGE,"E439")])]});
            extrude(context, id + "F32", {"entities" : qUnion([Q0]), "operationType" : NewBodyOperationType.REMOVE, "endBound" : BoundingType.UP_TO_SURFACE, "depth" : 25 * mm, "endBoundEntityFace" : qUnion([Q1]), "offsetDistance" : 25 * mm});
        }
    });
